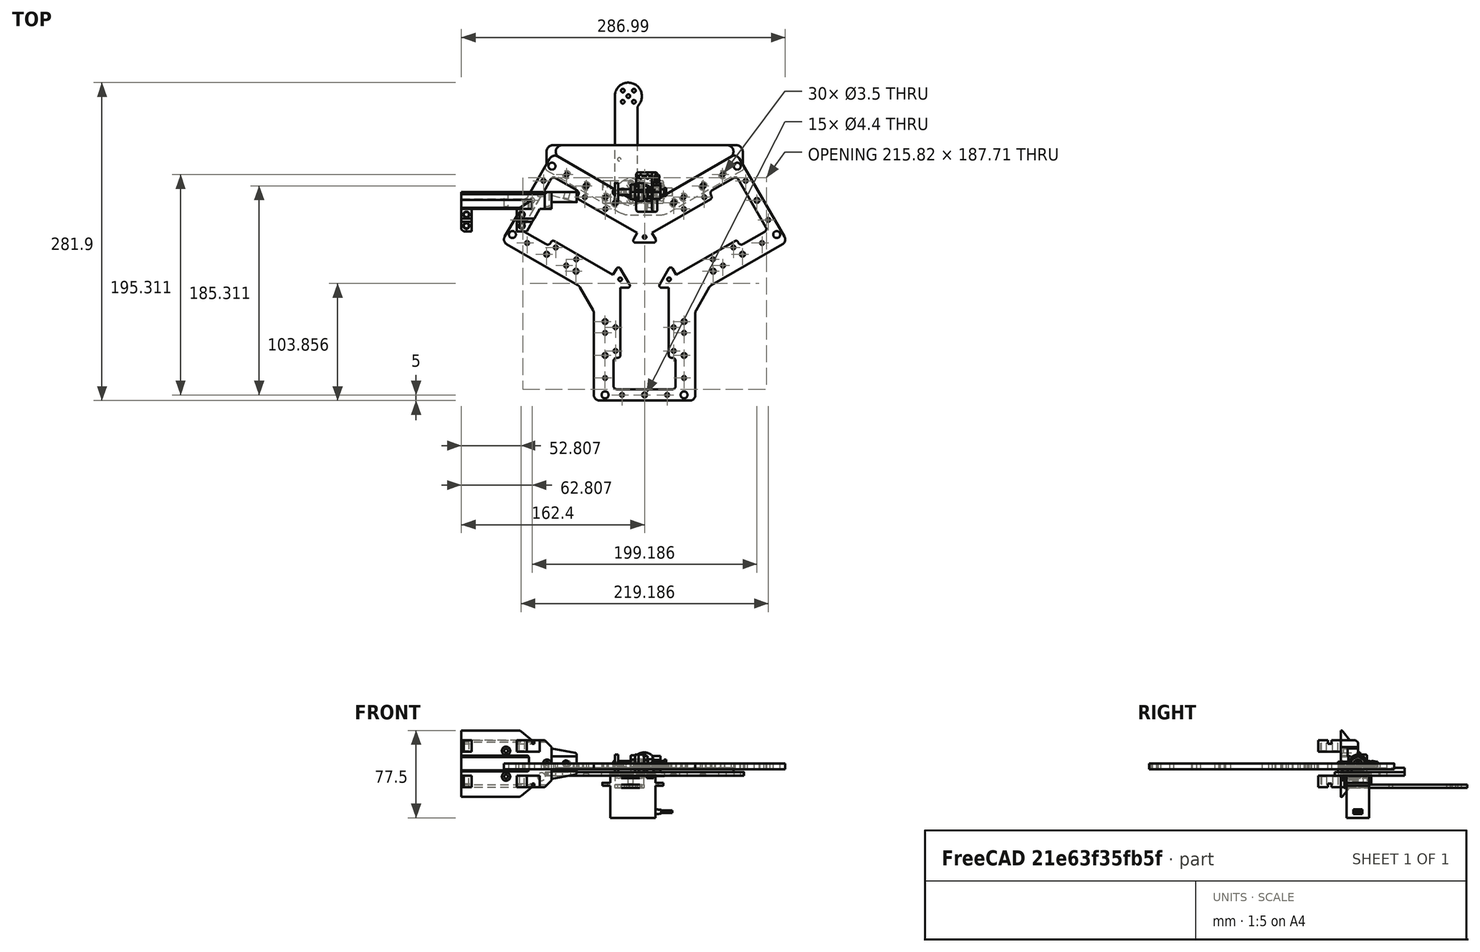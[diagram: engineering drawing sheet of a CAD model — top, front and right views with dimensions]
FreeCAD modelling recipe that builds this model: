
FCSTD DOCUMENT  (FreeCAD 1.2R20260204 (Git shallow))
Label: twin-actuator
License: All rights reserved
LicenseURL: https://en.wikipedia.org/wiki/All_rights_reserved
objects: Sketcher::SketchObject×46, App::Link×38, PartDesign::Pad×24, App::FeaturePython×22, App::Point×19, PartDesign::Pocket×17, PartDesign::Chamfer×17, PartDesign::Fillet×15, PartDesign::Body×13, PartDesign::Draft×6, PartDesign::Revolution×4, Assembly::JointGroup×3, Assembly::AssemblyObject×3, Part::FeaturePython×2, PartDesign::ShapeBinder×2, App::Part×2, PartDesign::SubShapeBinder×2, PartDesign::Mirrored×2, TechDraw::DrawProjGroupItem×2, PartDesign::LinearPattern×1, +5 more types
note: 367 computed .brp shape members not serialized (recipe doc carries the construction recipe); baked Part::Feature solids carry a one-line shape summary decoded from their .brp
EXTERNAL_REF file=linear-lifter.FCStd obj=Assembly
EXTERNAL_REF file=linear-lifter.FCStd obj=MGN9_225mm_Custom
EXTERNAL_REF file=linear-lifter.FCStd obj=ClipRail
EXTERNAL_REF file=linear-lifter.FCStd obj=ClipRail001
EXTERNAL_REF file=linear-lifter.FCStd obj=ClipRail002
EXTERNAL_REF file=linear-lifter.FCStd obj=Chariot
EXTERNAL_REF file=linear-lifter.FCStd obj=mgn9c
EXTERNAL_REF file=linear-lifter.FCStd obj=Body028
EXTERNAL_REF file=linear-lifter.FCStd obj=MF001
EXTERNAL_REF file=linear-lifter.FCStd obj=MF002
EXTERNAL_REF file=linear-lifter.FCStd obj=Bielle001
EXTERNAL_REF file=linear-lifter.FCStd obj=RoundServoHorn
EXTERNAL_REF file=linear-lifter.FCStd obj=ServoLifterSpacer
EXTERNAL_REF file=linear-lifter.FCStd obj=ServoLifterPlate
EXTERNAL_REF file=linear-lifter.FCStd obj=Bielle002
EXTERNAL_REF file=linear-lifter.FCStd obj=MG997
EXTERNAL_REF file=../../ECAD/color-sensor-2026/color-sensor-asm.FCStd obj=Part001

FEATURE [App::Point] Origin133  label="Origine001"
  Role = Origin
FEATURE [App::Point] Origin136  label="Origine004"
  Role = Origin
FEATURE [App::Point] Origin137  label="Origine005"
  Role = Origin
FEATURE [App::Point] Origin138  label="Origine006"
  Role = Origin
FEATURE [Part::FeaturePython] Screw  label="M3x10-Vis"  # WARN: FeaturePython — macro-defined, semantics opaque (R4)
  BaseObject = -> Body [Edge47]
  Diameter = 1
  Invert = false
  LeftHanded = false
  Length = 2
  LengthCustom = 10
  MatchOuter = false
  Offset = 3
  OffsetAngle = 0
  Placement = pos=(-26,-1.72853e-06,-7e-16) rot=(0,-1,0;1.5708rad)
  Thread = false
  Type = 85
FEATURE [Sketcher::SketchObject] Sketch
  ArcFitTolerance = 0
  AttachmentSupport = -> [XZ_Plane]
  ExternalTypes = [0]
  FullyConstrained = true
  MakeInternals = false
  MapMode = 5
  Placement = pos=(0,0,0) rot=(1,0,0;1.5708rad)
  sketch-geometry (14):
    g0: LineSegment StartX=0 StartY=2.5 StartZ=0 EndX=3 EndY=2.5 EndZ=0
    g1: LineSegment StartX=3 StartY=2.5 StartZ=0 EndX=3 EndY=3.5 EndZ=0
    g2: LineSegment StartX=3 StartY=3.5 StartZ=0 EndX=5 EndY=3.5 EndZ=0
    g3: LineSegment StartX=5 StartY=3.5 StartZ=0 EndX=5 EndY=1.5 EndZ=0
    g4: LineSegment StartX=5 StartY=1.5 StartZ=0 EndX=-9 EndY=1.5 EndZ=0
    g5: LineSegment StartX=-9 StartY=1.5 StartZ=0 EndX=-9 EndY=0 EndZ=0
    g6: LineSegment StartX=-9 StartY=0 StartZ=0 EndX=-37.5 EndY=0 EndZ=0
    g7: LineSegment StartX=-37.5 StartY=0 StartZ=0 EndX=-37.5 EndY=2.5 EndZ=0
    g8: LineSegment StartX=-37.5 StartY=2.5 StartZ=0 EndX=-11 EndY=2.5 EndZ=0
    g9: LineSegment StartX=-11 StartY=2.5 StartZ=0 EndX=-11 EndY=4 EndZ=0
    g10: LineSegment StartX=-11 StartY=4 StartZ=0 EndX=-7 EndY=4 EndZ=0
    g11: LineSegment StartX=-7 StartY=4 StartZ=0 EndX=-7 EndY=7.5 EndZ=0
    g12: LineSegment StartX=-7 StartY=7.5 StartZ=0 EndX=0 EndY=7.5 EndZ=0
    g13: LineSegment StartX=0 StartY=7.5 StartZ=0 EndX=0 EndY=2.5 EndZ=0
  constraints (42):
    c: PointOnObject(g0,g-2)
    c: Horizontal(g0)
    c: Coincident(g0,g1)
    c: Coincident(g1,g2)
    c: Horizontal(g2)
    c: Coincident(g2,g3)
    c: Vertical(g3)
    c: Coincident(g3,g4)
    c: Horizontal(g4)
    c: Coincident(g4,g5)
    c: Vertical(g5)
    c: Coincident(g5,g6)
    c: PointOnObject(g6,g-1)
    c: Horizontal(g6)
    c: Coincident(g6,g7)
    c: Vertical(g7)
    c: Coincident(g7,g8)
    c: Horizontal(g8)
    c: Coincident(g8,g9)
    c: Coincident(g9,g10)
    c: Horizontal(g10)
    c: Coincident(g10,g11)
    c: Vertical(g11)
    c: Coincident(g11,g12)
    c: Horizontal(g12)
    c: Coincident(g12,g13)
    c: Coincident(g13,g0)
    c: Vertical(g13)
    c: Vertical(g9)
    c: Vertical(g1)
    c: DistanceY(g2) = 3.5
    c: DistanceX(g2,g2) = 2
    c: DistanceX(g-1,g0) = 3
    c: DistanceY(g0) = 2.5
    c: DistanceX(g4,g4) = 14
    c: DistanceY(g3) = 1.5
    c: DistanceY(g10) = 4
    c: DistanceY(g12) = 7.5
    c: DistanceX(g12,g12) = 7
    c: DistanceX(g10,g10) = 4
    c: DistanceY(g8) = 2.5
    c: DistanceX(g6,g3) = 42.5
FEATURE [PartDesign::Revolution] Revolution
  Angle = 360
  Angle2 = 0
  Axis = (1,0,0)
  Base = (0,0,0)
  FuseOrder = 0
  Placement = pos=(0,0,0) rot=(1,0,0;1.5708rad)
  Profile = -> Sketch
  ReferenceAxis = -> X_Axis
  Refine = true
  Suppressed = false
  Type = 0
FEATURE [Sketcher::SketchObject] Sketch001
  ArcFitTolerance = 0
  AttachmentSupport = -> [YZ_Plane]
  ExternalGeometry = -> [Revolution]
  ExternalTypes = [0]
  FullyConstrained = true
  MakeInternals = false
  MapMode = 5
  Placement = pos=(0,0,0) rot=(0.57735,0.57735,0.57735;2.0944rad)
  sketch-geometry (7):
    g0: LineSegment StartX=6 StartY=3.4641 StartZ=0 EndX=0 EndY=6.9282 EndZ=0
    g1: LineSegment StartX=0 StartY=6.9282 StartZ=0 EndX=-6 EndY=3.4641 EndZ=0
    g2: LineSegment StartX=-6 StartY=3.4641 StartZ=0 EndX=-6 EndY=-3.4641 EndZ=0
    g3: LineSegment StartX=-6 StartY=-3.4641 StartZ=0 EndX=1.8723e-12 EndY=-6.9282 EndZ=0
    g4: LineSegment StartX=1.8723e-12 StartY=-6.9282 StartZ=0 EndX=6 EndY=-3.4641 EndZ=0
    g5: LineSegment StartX=6 StartY=-3.4641 StartZ=0 EndX=6 EndY=3.4641 EndZ=0
    g6: Circle [constr] CenterX=0 CenterY=0 CenterZ=0 NormalX=0 NormalY=0 NormalZ=1 AngleXU=0 Radius=6.9282
  constraints (16):
    c: Coincident(g0,g1)
    c: Coincident(g1,g2)
    c: Coincident(g2,g3)
    c: Coincident(g3,g4)
    c: Coincident(g4,g5)
    c: Coincident(g5,g0)
    c: Equal(g0, g1-g5) x5
    c: PointOnObject(g0,g6)
    c: PointOnObject(g1,g6)
    c: PointOnObject(g2,g6)
    c: PointOnObject(g3,g6)
    c: PointOnObject(g4,g6)
    c: PointOnObject(g5,g6)
    c: Coincident(g6,g-1)
    c: PointOnObject(g0,g-2)
    c: DistanceX(g1,g0) = 12
FEATURE [PartDesign::Pocket] Pocket
  BaseFeature = -> Revolution
  Direction = (-1,0,0)
  Length = 5
  Length2 = 100
  Placement = pos=(0,0,0) rot=(1,0,0;1.5708rad)
  Profile = -> Sketch001
  Refine = true
  SideType = 0
  Suppressed = false
  Type = 1
  Type2 = 0
FEATURE [Sketcher::SketchObject] Sketch002
  ArcFitTolerance = 0
  AttachmentSupport = -> [XZ_Plane]
  ExternalGeometry = -> [Pocket]
  ExternalTypes = [0]
  FullyConstrained = true
  MakeInternals = false
  MapMode = 5
  Placement = pos=(0,0,0) rot=(1,0,0;1.5708rad)
  sketch-geometry (2):
    g0: Circle CenterX=-3.5 CenterY=0 CenterZ=0 NormalX=0 NormalY=0 NormalZ=1 AngleXU=0 Radius=2.5
    g1: LineSegment [constr] StartX=-6e-16 StartY=-3.4641 StartZ=0 EndX=-7 EndY=3.4641 EndZ=0
  constraints (5):
    c: PointOnObject(g0,g-1)
    c: Diameter(g0) = 5
    c: Coincident(g1,g-4)
    c: Coincident(g1,g-3)
    c: PointOnObject(g0,g1)
FEATURE [PartDesign::Pocket] Pocket001
  BaseFeature = -> Pocket
  Direction = (0,1,-2e-16)
  Length = 5
  Length2 = 100
  Placement = pos=(0,0,0) rot=(1,0,0;1.5708rad)
  Profile = -> Sketch002
  Refine = true
  SideType = 2
  Suppressed = false
  Type = 1
  Type2 = 0
FEATURE [PartDesign::Chamfer] Chamfer
  Angle = 45
  Base = -> Pocket001 [Edge14,Edge21]
  BaseFeature = -> Pocket001
  ChamferType = 0
  FlipDirection = false
  Placement = pos=(0,0,0) rot=(1,0,0;1.5708rad)
  Refine = true
  Size = 0.2
  Size2 = 1
  SupportTransform = false
  Suppressed = false
  UseAllEdges = false
FEATURE [Sketcher::SketchObject] Sketch003
  ArcFitTolerance = 0
  AttachmentSupport = -> [Chamfer]
  ExternalTypes = [0]
  FullyConstrained = true
  MakeInternals = false
  MapMode = 5
  Placement = pos=(-37.5,0,0) rot=(0.707107,0,-0.707107;3.14159rad)
  sketch-geometry (1):
    g0: Circle CenterX=0 CenterY=0 CenterZ=0 NormalX=0 NormalY=0 NormalZ=1 AngleXU=0 Radius=1.5
  constraints (2):
    c: Coincident(g0,g-1)
    c: Diameter(g0) = 3
FEATURE [PartDesign::Pocket] Pocket002
  BaseFeature = -> Chamfer
  Direction = (1,0,2e-16)
  Length = 5
  Length2 = 100
  Placement = pos=(0,0,0) rot=(1,0,0;1.5708rad)
  Profile = -> Sketch003
  Refine = true
  SideType = 0
  Suppressed = false
  Type = 0
  Type2 = 0
FEATURE [PartDesign::Body] Body  label="Axe"
  AllowCompound = true
  Group = -> [Sketch,Revolution,Sketch001,Pocket,Sketch002,Pocket001,Chamfer,Sketch003,Pocket002]
  Origin = -> Origin105
  Placement = pos=(14.5,-1.72853e-06,0) rot=(0,0,1;0rad)
  Tip = -> Pocket002
FEATURE [Sketcher::SketchObject] Sketch004
  ArcFitTolerance = 0
  AttachmentSupport = -> [XY_Plane001]
  ExternalTypes = [0]
  FullyConstrained = true
  MakeInternals = false
  MapMode = 5
  sketch-geometry (10):
    g0: LineSegment StartX=-12 StartY=2.5 StartZ=0 EndX=-12 EndY=4 EndZ=0
    g1: LineSegment StartX=-12 StartY=4 StartZ=0 EndX=-2 EndY=4 EndZ=0
    g2: LineSegment StartX=-2 StartY=4 StartZ=0 EndX=-2 EndY=3.25 EndZ=0
    g3: LineSegment StartX=-2 StartY=3.25 StartZ=0 EndX=0 EndY=3.25 EndZ=0
    g4: LineSegment StartX=0 StartY=3.25 StartZ=0 EndX=0 EndY=7.5 EndZ=0
    g5: LineSegment StartX=0 StartY=7.5 StartZ=0 EndX=3 EndY=7.5 EndZ=0
    g6: LineSegment StartX=3 StartY=7.5 StartZ=0 EndX=3 EndY=4 EndZ=0
    g7: LineSegment StartX=-12 StartY=2.5 StartZ=0 EndX=3.5 EndY=2.5 EndZ=0
    g8: LineSegment StartX=3.5 StartY=2.5 StartZ=0 EndX=3.5 EndY=4 EndZ=0
    g9: LineSegment StartX=3.5 StartY=4 StartZ=0 EndX=3 EndY=4 EndZ=0
  constraints (30):
    c: Vertical(g0)
    c: Coincident(g0,g1)
    c: Horizontal(g1)
    c: Coincident(g1,g2)
    c: Coincident(g2,g3)
    c: Horizontal(g3)
    c: Coincident(g3,g4)
    c: Vertical(g4)
    c: Coincident(g4,g5)
    c: Horizontal(g5)
    c: Coincident(g5,g6)
    c: Vertical(g6)
    c: Vertical(g2)
    c: DistanceY(g5) = 7.5
    c: DistanceX(g5,g5) = 3
    c: DistanceX(g1,g1) = 10
    c: DistanceY(g3) = 3.25
    c: DistanceY(g1) = 4
    c: Coincident(g0,g7)
    c: Horizontal(g7)
    c: Coincident(g7,g8)
    c: Vertical(g8)
    c: Coincident(g8,g9)
    c: Coincident(g9,g6)
    c: Horizontal(g9)
    c: DistanceY(g7) = 2.5
    c: PointOnObject(g3,g-2)
    c: DistanceX(g0,g7) = 15.5
    c: DistanceX(g6,g8) = 0.5
    c: DistanceY(g8) = 4
FEATURE [PartDesign::Revolution] Revolution002
  Angle = 360
  Angle2 = 0
  Axis = (1,0,0)
  Base = (0,0,0)
  FuseOrder = 0
  Profile = -> Sketch004
  ReferenceAxis = -> X_Axis001
  Refine = true
  Suppressed = false
  Type = 0
FEATURE [Sketcher::SketchObject] Sketch005
  ArcFitTolerance = 0
  AttachmentSupport = -> [YZ_Plane001]
  ExternalGeometry = -> [Revolution002]
  ExternalTypes = [0]
  FullyConstrained = true
  MakeInternals = false
  MapMode = 5
  Placement = pos=(0,0,0) rot=(0.57735,0.57735,0.57735;2.0944rad)
  sketch-geometry (7):
    g0: LineSegment StartX=0 StartY=6.9282 StartZ=0 EndX=-6 EndY=3.4641 EndZ=0
    g1: LineSegment StartX=-6 StartY=3.4641 StartZ=0 EndX=-6 EndY=-3.4641 EndZ=0
    g2: LineSegment StartX=-6 StartY=-3.4641 StartZ=0 EndX=0 EndY=-6.9282 EndZ=0
    g3: LineSegment StartX=0 StartY=-6.9282 StartZ=0 EndX=6 EndY=-3.4641 EndZ=0
    g4: LineSegment StartX=6 StartY=-3.4641 StartZ=0 EndX=6 EndY=3.4641 EndZ=0
    g5: LineSegment StartX=6 StartY=3.4641 StartZ=0 EndX=0 EndY=6.9282 EndZ=0
    g6: Circle [constr] CenterX=0 CenterY=0 CenterZ=0 NormalX=0 NormalY=0 NormalZ=1 AngleXU=0 Radius=6.9282
  constraints (16):
    c: Coincident(g0,g1)
    c: Coincident(g1,g2)
    c: Coincident(g2,g3)
    c: Coincident(g3,g4)
    c: Coincident(g4,g5)
    c: Coincident(g5,g0)
    c: Equal(g0, g1-g5) x5
    c: PointOnObject(g0,g6)
    c: PointOnObject(g1,g6)
    c: PointOnObject(g2,g6)
    c: PointOnObject(g3,g6)
    c: PointOnObject(g4,g6)
    c: PointOnObject(g5,g6)
    c: Coincident(g6,g-1)
    c: PointOnObject(g5,g-2)
    c: DistanceX(g0,g4) = 12
FEATURE [PartDesign::Pocket] Pocket003
  BaseFeature = -> Revolution002
  Direction = (-1,0,0)
  Length = 5
  Length2 = 100
  Profile = -> Sketch005
  Refine = true
  Reversed = true
  SideType = 0
  Suppressed = false
  Type = 1
  Type2 = 0
FEATURE [PartDesign::Chamfer] Chamfer001
  Angle = 45
  Base = -> Pocket003 [Edge2,Edge5]
  BaseFeature = -> Pocket003
  ChamferType = 0
  FlipDirection = false
  Refine = true
  Size = 0.3
  Size2 = 1
  SupportTransform = false
  Suppressed = false
  UseAllEdges = false
FEATURE [PartDesign::Body] Body001  label="Coulisse"
  AllowCompound = true
  Group = -> [Sketch004,Revolution002,Sketch005,Pocket003,Chamfer001]
  Origin = -> Origin001
  Placement = pos=(-3.8147e-06,9.095e-13,0) rot=(0,0,1;0rad)
  Tip = -> Chamfer001
FEATURE [Sketcher::SketchObject] Sketch006
  ArcFitTolerance = 0
  AttachmentSupport = -> [XY_Plane002]
  ExternalTypes = [0]
  FullyConstrained = true
  MakeInternals = false
  MapMode = 5
  sketch-geometry (10):
    g0: LineSegment StartX=0 StartY=-4.5 StartZ=0 EndX=-2.5 EndY=-4.5 EndZ=0
    g1: LineSegment StartX=-2.5 StartY=-4.5 StartZ=0 EndX=-2.5 EndY=-1 EndZ=0
    g2: LineSegment StartX=-2.5 StartY=-1 StartZ=0 EndX=-2 EndY=-1 EndZ=0
    g3: LineSegment StartX=-2 StartY=-1 StartZ=0 EndX=-2 EndY=0 EndZ=0
    g4: LineSegment StartX=-2 StartY=0 StartZ=0 EndX=-4 EndY=0 EndZ=0
    g5: LineSegment StartX=-4 StartY=0 StartZ=0 EndX=-4 EndY=2.5 EndZ=0
    g6: LineSegment StartX=-4 StartY=2.5 StartZ=0 EndX=-2 EndY=2.5 EndZ=0
    g7: LineSegment StartX=-2 StartY=2.5 StartZ=0 EndX=-2 EndY=3.5 EndZ=0
    g8: LineSegment StartX=-2 StartY=3.5 StartZ=0 EndX=0 EndY=3.5 EndZ=0
    g9: LineSegment StartX=0 StartY=3.5 StartZ=0 EndX=0 EndY=-4.5 EndZ=0
  constraints (30):
    c: Horizontal(g0)
    c: Coincident(g0,g1)
    c: Vertical(g1)
    c: Coincident(g1,g2)
    c: Horizontal(g2)
    c: Coincident(g2,g3)
    c: PointOnObject(g3,g-1)
    c: Vertical(g3)
    c: Coincident(g3,g4)
    c: PointOnObject(g4,g-1)
    c: Coincident(g4,g5)
    c: Vertical(g5)
    c: Coincident(g5,g6)
    c: Horizontal(g6)
    c: Coincident(g6,g7)
    c: Vertical(g7)
    c: Coincident(g7,g8)
    c: Horizontal(g8)
    c: Coincident(g8,g9)
    c: Coincident(g9,g0)
    c: Vertical(g9)
    c: DistanceY(g5) = 2.5
    c: DistanceX(g3,g-1) = 2
    c: DistanceX(g0,g-1) = 2.5
    c: DistanceX(g4,g-1) = 4
    c: DistanceY(g7,g7) = 1
    c: DistanceY(g3,g3) = 1
    c: DistanceY(g0,g6) = 7
    c: DistanceX(g7,g-1) = 2
    c: PointOnObject(g0,g-2)
FEATURE [PartDesign::Revolution] Revolution003
  Angle = 360
  Angle2 = 0
  Axis = (0,1,0)
  Base = (0,0,0)
  FuseOrder = 0
  Profile = -> Sketch006
  ReferenceAxis = -> Sketch006 [V_Axis]
  Refine = true
  Suppressed = false
  Type = 0
FEATURE [Sketcher::SketchObject] Sketch007
  ArcFitTolerance = 0
  AttachmentSupport = -> [XY_Plane002]
  ExternalTypes = [0]
  FullyConstrained = true
  MakeInternals = false
  MapMode = 5
FEATURE [Sketcher::SketchObject] Sketch008
  ArcFitTolerance = 0
  AttachmentSupport = -> [XY_Plane002]
  ExternalGeometry = -> [Revolution003]
  ExternalTypes = [0]
  FullyConstrained = true
  MakeInternals = false
  MapMode = 5
  sketch-geometry (5):
    g0: LineSegment StartX=0 StartY=3.5 StartZ=0 EndX=-2.5 EndY=3.5 EndZ=0
    g1: LineSegment StartX=-2.5 StartY=3.5 StartZ=0 EndX=-2.5 EndY=4.5 EndZ=0
    g2: LineSegment StartX=-2.5 StartY=4.5 StartZ=0 EndX=-2 EndY=6.5 EndZ=0
    g3: LineSegment StartX=-2 StartY=6.5 StartZ=0 EndX=0 EndY=6.5 EndZ=0
    g4: LineSegment StartX=0 StartY=6.5 StartZ=0 EndX=0 EndY=3.5 EndZ=0
  constraints (15):
    c: PointOnObject(g0,g-2)
    c: Horizontal(g0)
    c: Coincident(g0,g1)
    c: Coincident(g1,g2)
    c: Coincident(g2,g3)
    c: PointOnObject(g3,g-2)
    c: Horizontal(g3)
    c: Coincident(g3,g4)
    c: Coincident(g0,g4)
    c: PointOnObject(g0,g-3)
    c: DistanceX(g0,g-1) = 2.5
    c: Vertical(g1)
    c: DistanceY(g4,g4) = 3
    c: DistanceX(g2,g0) = 2
    c: DistanceY(g1,g1) = 1
FEATURE [PartDesign::Revolution] Revolution004
  Angle = 360
  Angle2 = 0
  Axis = (0,1,0)
  Base = (0,0,0)
  BaseFeature = -> Revolution003
  FuseOrder = 0
  Profile = -> Sketch008
  ReferenceAxis = -> Sketch008 [V_Axis]
  Refine = true
  Suppressed = false
  Type = 0
FEATURE [PartDesign::LinearPattern] LinearPattern001
  BaseFeature = -> Revolution004
  Direction = -> Y_Axis002
  Length = 3
  Length2 = 100
  Mode = 0
  Mode2 = 0
  Occurrences = 2
  Occurrences2 = 1
  Offset = 3
  Offset2 = 10
  Originals = -> [Revolution004]
  Refine = true
  Reversed2 = false
  SpacingPattern = [0]
  SpacingPattern2 = [0]
  Spacings = [-1]
  Suppressed = false
  TransformMode = 0
FEATURE [Sketcher::SketchObject] Sketch009
  ArcFitTolerance = 0
  AttachmentSupport = -> [XZ_Plane002]
  ExternalTypes = [0]
  FullyConstrained = true
  MakeInternals = false
  MapMode = 5
  Placement = pos=(0,0,0) rot=(1,0,0;1.5708rad)
  sketch-geometry (1):
    g0: Circle CenterX=0 CenterY=0 CenterZ=0 NormalX=0 NormalY=0 NormalZ=1 AngleXU=0 Radius=1.5
  constraints (2):
    c: Coincident(g0,g-1)
    c: Diameter(g0) = 3
FEATURE [PartDesign::Pocket] Pocket004
  BaseFeature = -> LinearPattern001
  Direction = (0,1,-2e-16)
  Length = 5
  Length2 = 100
  Profile = -> Sketch009
  Refine = true
  SideType = 2
  Suppressed = false
  Type = 1
  Type2 = 0
FEATURE [PartDesign::Chamfer] Chamfer002
  Angle = 45
  Base = -> Pocket004 [Edge1,Edge3]
  BaseFeature = -> Pocket004
  ChamferType = 0
  FlipDirection = false
  Refine = true
  Size = 0.3
  Size2 = 1
  SupportTransform = false
  Suppressed = false
  UseAllEdges = false
FEATURE [Sketcher::SketchObject] Sketch010
  ArcFitTolerance = 0
  AttachmentSupport = -> [XZ_Plane002]
  ExternalGeometry = -> [Chamfer002]
  ExternalTypes = [0]
  FullyConstrained = true
  MakeInternals = false
  MapMode = 5
  Placement = pos=(0,0,0) rot=(1,0,0;1.5708rad)
  sketch-geometry (7):
    g0: LineSegment StartX=0 StartY=3.4641 StartZ=0 EndX=-3 EndY=1.73205 EndZ=0
    g1: LineSegment StartX=-3 StartY=1.73205 StartZ=0 EndX=-3 EndY=-1.73205 EndZ=0
    g2: LineSegment StartX=-3 StartY=-1.73205 StartZ=0 EndX=-5.997e-12 EndY=-3.4641 EndZ=0
    g3: LineSegment StartX=-5.997e-12 StartY=-3.4641 StartZ=0 EndX=3 EndY=-1.73205 EndZ=0
    g4: LineSegment StartX=3 StartY=-1.73205 StartZ=0 EndX=3 EndY=1.73205 EndZ=0
    g5: LineSegment StartX=3 StartY=1.73205 StartZ=0 EndX=0 EndY=3.4641 EndZ=0
    g6: Circle [constr] CenterX=0 CenterY=0 CenterZ=0 NormalX=0 NormalY=0 NormalZ=1 AngleXU=0 Radius=3.4641
  constraints (16):
    c: Coincident(g0,g1)
    c: Coincident(g1,g2)
    c: Coincident(g2,g3)
    c: Coincident(g3,g4)
    c: Coincident(g4,g5)
    c: Coincident(g5,g0)
    c: Equal(g0, g1-g5) x5
    c: PointOnObject(g0,g6)
    c: PointOnObject(g1,g6)
    c: PointOnObject(g2,g6)
    c: PointOnObject(g3,g6)
    c: PointOnObject(g4,g6)
    c: PointOnObject(g5,g6)
    c: Coincident(g6,g-1)
    c: PointOnObject(g0,g-2)
    c: DistanceX(g0,g4) = 6
FEATURE [PartDesign::Pocket] Pocket005
  BaseFeature = -> Chamfer002
  Direction = (0,1,-2e-16)
  Length = 5
  Length2 = 100
  Profile = -> Sketch010
  Refine = true
  SideType = 0
  Suppressed = false
  Type = 1
  Type2 = 0
FEATURE [PartDesign::Body] Body002  label="ConnecteurPneu"
  AllowCompound = true
  Group = -> [Sketch006,Revolution003,Sketch007,Sketch008,Revolution004,LinearPattern001,Sketch009,Pocket004,Chamfer002,Sketch010,Pocket005]
  Origin = -> Origin002
  Placement = pos=(11,6,0) rot=(0,0,1;0rad)
  Tip = -> Pocket005
FEATURE [Sketcher::SketchObject] Sketch013
  ArcFitTolerance = 0
  AttachmentSupport = -> [YZ_Plane005]
  ExternalTypes = [0]
  FullyConstrained = true
  MakeInternals = false
  MapMode = 5
  Placement = pos=(0,0,0) rot=(0.57735,0.57735,0.57735;2.0944rad)
  sketch-geometry (5):
    g0: Circle CenterX=0 CenterY=0 CenterZ=0 NormalX=0 NormalY=0 NormalZ=1 AngleXU=0 Radius=1.6
    g1: ArcOfCircle CenterX=0 CenterY=0 CenterZ=0 NormalX=0 NormalY=0 NormalZ=1 AngleXU=0 Radius=8 StartAngle=0 EndAngle=3.14159
    g2: LineSegment StartX=-8 StartY=1e-15 StartZ=0 EndX=-8 EndY=-8 EndZ=0
    g3: LineSegment StartX=-8 StartY=-8 StartZ=0 EndX=8 EndY=-8 EndZ=0
    g4: LineSegment StartX=8 StartY=-8 StartZ=0 EndX=8 EndY=0 EndZ=0
  constraints (14):
    c: Coincident(g0,g-1)
    c: Diameter(g0) = 3.2
    c: Coincident(g1,g0)
    c: PointOnObject(g1,g-1)
    c: PointOnObject(g1,g-1)
    c: Coincident(g2,g1)
    c: Vertical(g2)
    c: Horizontal(g3)
    c: Coincident(g3,g4)
    c: Coincident(g4,g1)
    c: Vertical(g4)
    c: Coincident(g2,g3)
    c: Diameter(g1) = 16
    c: DistanceY(g3) = -8
FEATURE [PartDesign::Pad] Pad002
  Direction = (1,0,0)
  Length = 3
  Length2 = 100
  Placement = pos=(0,0,0) rot=(0.57735,0.57735,0.57735;2.0944rad)
  Profile = -> Sketch013
  Refine = true
  SideType = 0
  Suppressed = false
  Type = 0
  Type2 = 0
FEATURE [PartDesign::Fillet] Fillet001
  Base = -> Pad002 [Edge8,Edge5]
  BaseFeature = -> Pad002
  Placement = pos=(0,0,0) rot=(0.57735,0.57735,0.57735;2.0944rad)
  Radius = 1
  Refine = true
  SupportTransform = false
  Suppressed = false
  UseAllEdges = false
FEATURE [PartDesign::Body] Body004  label="ContreRotation"
  AllowCompound = true
  Group = -> [Sketch013,Pad002,Fillet001]
  Origin = -> Origin006
  Placement = pos=(-26,-2.62261e-06,3.05176e-05) rot=(1,0,0;1.5708rad)
  Tip = -> Fillet001
FEATURE [App::Point] Origin140  label="Origine007"
  Role = Origin
FEATURE [Sketcher::SketchObject] Sketch014
  ArcFitTolerance = 0
  AttachmentSupport = -> [YZ_Plane087]
  ExternalTypes = [0]
  FullyConstrained = true
  MakeInternals = false
  MapMode = 5
  Placement = pos=(0,0,0) rot=(0.57735,0.57735,0.57735;2.0944rad)
  sketch-geometry (5):
    g0: ArcOfCircle CenterX=0 CenterY=0 CenterZ=0 NormalX=0 NormalY=0 NormalZ=1 AngleXU=0 Radius=8 StartAngle=2e-16 EndAngle=3.14159
    g1: LineSegment StartX=-8 StartY=4.01e-14 StartZ=0 EndX=-8 EndY=-8 EndZ=0
    g2: LineSegment StartX=-8 StartY=-8 StartZ=0 EndX=8 EndY=-8 EndZ=0
    g3: LineSegment StartX=8 StartY=-8 StartZ=0 EndX=8 EndY=1.8e-15 EndZ=0
    g4: Circle CenterX=0 CenterY=0 CenterZ=0 NormalX=0 NormalY=0 NormalZ=1 AngleXU=0 Radius=4.15
  constraints (14):
    c: Coincident(g0,g-1)
    c: PointOnObject(g0,g-1)
    c: PointOnObject(g0,g-1)
    c: Coincident(g1,g0)
    c: Coincident(g1,g2)
    c: Horizontal(g2)
    c: Coincident(g2,g3)
    c: Coincident(g3,g0)
    c: Vertical(g3)
    c: Vertical(g1)
    c: Diameter(g0) = 16
    c: DistanceY(g2) = -8
    c: Coincident(g4,g0)
    c: Diameter(g4) = 8.3
FEATURE [PartDesign::Pad] Pad003
  Direction = (1,0,0)
  Length = 8
  Length2 = 100
  Placement = pos=(0,0,0) rot=(0.57735,0.57735,0.57735;2.0944rad)
  Profile = -> Sketch014
  ReferenceAxis = -> Sketch014 [N_Axis]
  Refine = true
  Reversed = true
  SideType = 0
  Suppressed = false
  Type = 0
  Type2 = 0
FEATURE [Sketcher::SketchObject] Sketch015
  ArcFitTolerance = 0
  AttachmentSupport = -> [Pad003]
  ExternalGeometry = -> [Pad003]
  ExternalTypes = [0]
  FullyConstrained = true
  MakeInternals = false
  MapMode = 5
  Placement = pos=(0,-1.8e-15,-8) rot=(0.707107,0.707107,0;3.14159rad)
  sketch-geometry (19):
    g0: LineSegment StartX=-8 StartY=-26 StartZ=0 EndX=8 EndY=-26 EndZ=0
    g1: Circle [constr] CenterX=0 CenterY=-12 CenterZ=0 NormalX=0 NormalY=0 NormalZ=1 AngleXU=0 Radius=10
    g2: LineSegment [constr] StartX=-8 StartY=0 StartZ=0 EndX=8 EndY=0 EndZ=0
    g3: LineSegment StartX=-8 StartY=0 StartZ=0 EndX=-8 EndY=-3.05573 EndZ=0
    g4: LineSegment StartX=8 StartY=0 StartZ=0 EndX=8 EndY=-3.05573 EndZ=0
    g5: LineSegment StartX=8 StartY=-26 StartZ=0 EndX=8 EndY=-20.9443 EndZ=0
    g6: LineSegment StartX=-8 StartY=-26 StartZ=0 EndX=-8 EndY=-20.9443 EndZ=0
    g7: ArcOfCircle CenterX=0 CenterY=-12 CenterZ=0 NormalX=0 NormalY=0 NormalZ=1 AngleXU=0 Radius=12 StartAngle=2.30052 EndAngle=3.98266
    g8: ArcOfCircle CenterX=0 CenterY=-12 CenterZ=0 NormalX=0 NormalY=0 NormalZ=1 AngleXU=0 Radius=12 StartAngle=5.44212 EndAngle=7.12425
    g9: Circle CenterX=-7 CenterY=-12 CenterZ=0 NormalX=0 NormalY=0 NormalZ=1 AngleXU=0 Radius=2.25
    g10: Circle CenterX=7 CenterY=-12 CenterZ=0 NormalX=0 NormalY=0 NormalZ=1 AngleXU=0 Radius=2.25
    g11: Circle [constr] CenterX=0 CenterY=-19 CenterZ=0 NormalX=0 NormalY=0 NormalZ=1 AngleXU=0 Radius=2.25
    g12: Circle [constr] CenterX=0 CenterY=-5 CenterZ=0 NormalX=0 NormalY=0 NormalZ=1 AngleXU=0 Radius=2.25
    g13: Circle [constr] CenterX=0 CenterY=-12 CenterZ=0 NormalX=0 NormalY=0 NormalZ=1 AngleXU=0 Radius=7
    g14: LineSegment [constr] StartX=-7 StartY=-12 StartZ=0 EndX=7 EndY=-12 EndZ=0
    g15: Circle [constr] CenterX=0 CenterY=-12 CenterZ=0 NormalX=0 NormalY=0 NormalZ=1 AngleXU=0 Radius=2.25
    g16: LineSegment StartX=-8 StartY=0 StartZ=0 EndX=-8 EndY=18 EndZ=0
    g17: LineSegment StartX=-8 StartY=18 StartZ=0 EndX=8 EndY=18 EndZ=0
    g18: LineSegment StartX=8 StartY=18 StartZ=0 EndX=8 EndY=0 EndZ=0
  constraints (51):
    c: Symmetric(g0,g0,g-2)
    c: DistanceY(g0,g-1) = 26
    c: PointOnObject(g1,g-2)
    c: DistanceY(g1,g-1) = 12
    c: Diameter(g1) = 20
    c: PointOnObject(g2,g-1)
    c: Equal(g0,g2)
    c: Symmetric(g2,g2,g-2)
    c: Coincident(g2,g3)
    c: Vertical(g3)
    c: Coincident(g2,g4)
    c: Vertical(g4)
    c: Coincident(g0,g5)
    c: Vertical(g5)
    c: Coincident(g0,g6)
    c: Vertical(g6)
    c: Coincident(g7,g1)
    c: Coincident(g7,g3)
    c: Coincident(g7,g6)
    c: Coincident(g8,g7)
    c: Coincident(g8,g4)
    c: Coincident(g8,g5)
    c: DistanceX(g2,g2) = 16
    c: Diameter(g8) = 24
    c: PointOnObject(g11,g-2)
    c: PointOnObject(g12,g-2)
    c: Coincident(g13,g7)
    c: PointOnObject(g12,g13)
    c: PointOnObject(g10,g13)
    c: PointOnObject(g11,g13)
    c: PointOnObject(g9,g13)
    c: Diameter(g13) = 14
    c: Diameter(g12) = 4.5
    c: Equal(g12,g11)
    c: Equal(g12,g10)
    c: Equal(g12,g9)
    c: Coincident(g14,g9)
    c: Coincident(g14,g10)
    c: Horizontal(g14)
    c: PointOnObject(g7,g14)
    c: Equal(g3,g4)
    c: Coincident(g15,g7)
    c: Equal(g15,g10)
    c: Coincident(g16,g2)
    c: Vertical(g16)
    c: Coincident(g17,g16)
    c: Horizontal(g17)
    c: Coincident(g18,g17)
    c: Coincident(g18,g2)
    c: Vertical(g18)
    c: DistanceY(g18,g18) = 18
FEATURE [PartDesign::Pad] Pad004
  BaseFeature = -> Pad003
  Direction = (0,0,-1)
  Length = 10.5
  Length2 = 100
  Placement = pos=(0,0,0) rot=(0.57735,0.57735,0.57735;2.0944rad)
  Profile = -> Sketch015
  ReferenceAxis = -> Sketch015 [N_Axis]
  Refine = true
  SideType = 0
  Suppressed = false
  Type = 0
  Type2 = 0
FEATURE [PartDesign::Chamfer] Chamfer004
  Angle = 45
  Base = -> Pad004 [Edge20,Edge21,Edge38,Edge39]
  BaseFeature = -> Pad004
  ChamferType = 0
  FlipDirection = false
  Placement = pos=(0,0,0) rot=(0.57735,0.57735,0.57735;2.0944rad)
  Refine = true
  Size = 0.4
  Size2 = 1
  SupportTransform = false
  Suppressed = false
  UseAllEdges = false
FEATURE [PartDesign::Fillet] Fillet002
  Base = -> Chamfer004 [Edge35,Edge13,Edge28,Edge22,Edge20,Edge18,Edge16,Edge14]
  BaseFeature = -> Chamfer004
  Placement = pos=(0,0,0) rot=(0.57735,0.57735,0.57735;2.0944rad)
  Radius = 3
  Refine = true
  SupportTransform = false
  Suppressed = false
  UseAllEdges = false
FEATURE [Part::FeaturePython] Nut001  label="M8-Écrou004"  # WARN: FeaturePython — macro-defined, semantics opaque (R4)
  Diameter = 9
  Invert = true
  LeftHanded = false
  MatchOuter = false
  Offset = 5
  OffsetAngle = 0
  Placement = pos=(-8,3.3e-15,-2.8e-15) rot=(0,1,0;4.71239rad)
  Thread = false
  Type = 34
FEATURE [App::Point] Origin145  label="Origine012"
  Role = Origin
FEATURE [App::Point] Origin147  label="Origine014"
  Role = Origin
FEATURE [App::Link] SupportBras  label="SupportBras001"
  LinkPlacement = pos=(-79.6462,173.8,8.60566) rot=(-0.17215,0.356817,0.918175;3.59264rad)
  LinkedObject = -> Body005
  Placement = pos=(-79.6462,173.8,8.60566) rot=(-0.17215,0.356817,0.918175;3.59264rad)
FEATURE [App::Link] M8_Écrou004  label="M8-Écrou005"
  LinkPlacement = pos=(-69.522,180.003,10.343) rot=(0.617012,-0.780266,-0.102382;1.72836rad)
  LinkedObject = -> Nut001
  Placement = pos=(-69.522,180.003,10.343) rot=(0.617012,-0.780266,-0.102382;1.72836rad)
FEATURE [App::Link] Coulisse  label="Coulisse001"
  LinkPlacement = pos=(-79.6462,173.8,8.60566) rot=(-0.304533,-0.169428,0.937312;4.26313rad)
  LinkedObject = -> Body001
  Placement = pos=(-79.6462,173.8,8.60566) rot=(-0.304533,-0.169428,0.937312;4.26313rad)
FEATURE [App::Link] ConnecteurPneu  label="ConnecteurPneu001"
  LinkPlacement = pos=(-73.7107,180.292,16.9935) rot=(-0.215277,0.690739,0.690316;3.56562rad)
  LinkedObject = -> Body002
  Placement = pos=(-73.7107,180.292,16.9935) rot=(-0.215277,0.690739,0.690316;3.56562rad)
FEATURE [App::Link] Axe  label="Axe001"
  LinkPlacement = pos=(-70.8294,182.278,10.993) rot=(0.915071,0.285192,-0.285151;4.62314rad)
  LinkedObject = -> Body
  Placement = pos=(-70.8294,182.278,10.993) rot=(0.915071,0.285192,-0.285151;4.62314rad)
FEATURE [App::Link] ContreRotation  label="ContreRotation001"
  LinkPlacement = pos=(-101.687,160.969,10.998) rot=(-2.2e-05,0.000306,1;3.74597rad)
  LinkedObject = -> Body004
  Placement = pos=(-101.687,160.969,10.998) rot=(-2.2e-05,0.000306,1;3.74597rad)
FEATURE [App::Link] M3x10_Vis  label="M3x10-Vis001"
  LinkPlacement = pos=(-104.155,159.264,10.9984) rot=(0.802998,-0.421624,-0.421222;1.78804rad)
  LinkedObject = -> Screw
  Placement = pos=(-104.155,159.264,10.9984) rot=(0.802998,-0.421624,-0.421222;1.78804rad)
FEATURE [PartDesign::ShapeBinder] ShapeBinder
  Placement = pos=(3.5e-15,-1.2e-15,-10.5) rot=(0,0,1;0rad)
  Support = -> [Fillet002]
  TraceSupport = false
FEATURE [Sketcher::SketchObject] Sketch016
  ArcFitTolerance = 1e-06
  AttachmentSupport = -> [ShapeBinder]
  ExternalGeometry = -> [ShapeBinder]
  ExternalTypes = [0,0,0]
  FullyConstrained = true
  MakeInternals = false
  MapMode = 5
  Placement = pos=(3.5e-15,-1.2e-15,-18.5) rot=(1,0,0;3.14159rad)
  sketch-geometry (2):
    g0: Circle CenterX=-12 CenterY=7 CenterZ=0 NormalX=0 NormalY=0 NormalZ=1 AngleXU=0 Radius=1.6
    g1: Circle CenterX=-12 CenterY=-7 CenterZ=0 NormalX=0 NormalY=0 NormalZ=1 AngleXU=0 Radius=1.6
  constraints (4):
    c: Coincident(g0,g-21)
    c: Coincident(g1,g-22)
    c: Equal(g1,g0)
    c: Diameter(g0) = 3.2
FEATURE [PartDesign::Pad] Pad005
  Direction = (0,0,-1)
  Length = 3
  Length2 = 10
  Placement = pos=(3.5e-15,-1.2e-15,-10.5) rot=(0,0,1;0rad)
  Profile = -> Sketch016
  ReferenceAxis = -> Sketch016 [N_Axis]
  Refine = true
  SideType = 0
  Suppressed = false
  Type = 0
  Type2 = 0
FEATURE [Sketcher::SketchObject] Sketch017
  ArcFitTolerance = 1e-06
  AttachmentSupport = -> [Pad005]
  ExternalGeometry = -> [Pad005]
  ExternalTypes = [0,0,0]
  FullyConstrained = true
  MakeInternals = false
  MapMode = 5
  Placement = pos=(3.5e-15,-1.2e-15,-21.5) rot=(1,0,0;3.14159rad)
  sketch-geometry (16):
    g0: LineSegment StartX=-26 StartY=-5 StartZ=0 EndX=-26 EndY=-85 EndZ=0
    g1: LineSegment StartX=-6 StartY=-10.3923 StartZ=0 EndX=-6 EndY=-76.0557 EndZ=0
    g2: ArcOfCircle CenterX=-12 CenterY=-9e-16 CenterZ=0 NormalX=0 NormalY=0 NormalZ=1 AngleXU=0 Radius=12 StartAngle=3.57137 EndAngle=5.23599
    g3: LineSegment StartX=-22.9087 StartY=-5 StartZ=0 EndX=-26 EndY=-5 EndZ=0
    g4: ArcOfCircle CenterX=-14 CenterY=-85 CenterZ=0 NormalX=0 NormalY=0 NormalZ=1 AngleXU=0 Radius=12 StartAngle=3.14159 EndAngle=7.12425
    g5: Circle CenterX=-14 CenterY=-85 CenterZ=0 NormalX=0 NormalY=0 NormalZ=1 AngleXU=0 Radius=1.6
    g6: Circle [constr] CenterX=-14 CenterY=-85 CenterZ=0 NormalX=0 NormalY=0 NormalZ=1 AngleXU=0 Radius=7
    g7: LineSegment [constr] StartX=-9.05025 StartY=-80.0503 StartZ=0 EndX=-18.9497 EndY=-80.0503 EndZ=0
    g8: LineSegment [constr] StartX=-18.9497 StartY=-80.0503 StartZ=0 EndX=-18.9497 EndY=-89.9497 EndZ=0
    g9: LineSegment [constr] StartX=-18.9497 StartY=-89.9497 StartZ=0 EndX=-9.05025 EndY=-89.9497 EndZ=0
    g10: LineSegment [constr] StartX=-9.05025 StartY=-89.9497 StartZ=0 EndX=-9.05025 EndY=-80.0503 EndZ=0
    g11: Circle [constr] CenterX=-14 CenterY=-85 CenterZ=0 NormalX=0 NormalY=0 NormalZ=1 AngleXU=0 Radius=7
    g12: Circle CenterX=-18.9497 CenterY=-80.0503 CenterZ=0 NormalX=0 NormalY=0 NormalZ=1 AngleXU=0 Radius=1.6
    g13: Circle CenterX=-9.05025 CenterY=-80.0503 CenterZ=0 NormalX=0 NormalY=0 NormalZ=1 AngleXU=0 Radius=1.6
    g14: Circle CenterX=-9.05025 CenterY=-89.9497 CenterZ=0 NormalX=0 NormalY=0 NormalZ=1 AngleXU=0 Radius=1.6
    g15: Circle CenterX=-18.9497 CenterY=-89.9497 CenterZ=0 NormalX=0 NormalY=0 NormalZ=1 AngleXU=0 Radius=1.6
  constraints (40):
    c: Coincident(g0,g-3)
    c: Vertical(g0)
    c: PointOnObject(g1,g-4)
    c: Vertical(g1)
    c: Coincident(g2,g-4)
    c: Coincident(g2,g1)
    c: Coincident(g3,g2)
    c: Coincident(g3,g0)
    c: Horizontal(g3)
    c: Coincident(g4,g1)
    c: Tangent(g4,g0) = -1.5708
    c: Radius(g4) = 12
    c: Distance(g0,g1) = 20
    c: DistanceY(g4,g2) = 85
    c: Coincident(g5,g4)
    c: Coincident(g6,g4)
    c: Diameter(g5) = 3.2
    c: Coincident(g7,g8)
    c: Coincident(g8,g9)
    c: Coincident(g9,g10)
    c: Coincident(g10,g7)
    c: Equal(g7,g8)
    c: Equal(g7,g9)
    c: Equal(g7,g10)
    c: PointOnObject(g7,g11)
    c: PointOnObject(g8,g11)
    c: PointOnObject(g9,g11)
    c: PointOnObject(g10,g11)
    c: Coincident(g11,g4)
    c: PointOnObject(g10,g6)
    c: Horizontal(g7)
    c: Coincident(g12,g7)
    c: Coincident(g13,g7)
    c: Coincident(g14,g9)
    c: Coincident(g15,g8)
    c: Equal(g15,g14)
    c: Equal(g14,g13)
    c: Equal(g13,g12)
    c: Equal(g12,g5)
    c: Diameter(g6) = 14
FEATURE [PartDesign::Pad] Pad006
  BaseFeature = -> Pad005
  Direction = (0,0,-1)
  Length = 3
  Length2 = 10
  Placement = pos=(3.5e-15,-1.2e-15,-10.5) rot=(0,0,1;0rad)
  Profile = -> Sketch017
  ReferenceAxis = -> Sketch017 [N_Axis]
  Refine = true
  Reversed = true
  SideType = 0
  Suppressed = false
  Type = 0
  Type2 = 0
FEATURE [PartDesign::Fillet] Fillet003
  Base = -> Pad006 [Edge26,Edge38]
  BaseFeature = -> Pad006
  Placement = pos=(3.5e-15,-1.2e-15,-10.5) rot=(0,0,1;0rad)
  Radius = 6
  Refine = true
  SupportTransform = false
  Suppressed = false
  UseAllEdges = false
FEATURE [App::Link] arm_plate  label="arm-plate001"
  LinkPlacement = pos=(-74.8464,158.801,10.5635) rot=(-0.150356,-0.119638,0.981366;3.67771rad)
  LinkedObject = -> Body006
  Placement = pos=(-74.8464,158.801,10.5635) rot=(-0.150356,-0.119638,0.981366;3.67771rad)
FEATURE [App::Point] Origin081  label="Origine016"
  Role = Origin
FEATURE [App::Point] Origin082  label="Origine017"
  Role = Origin
FEATURE [App::Point] Origin083  label="Origine018"
  Role = Origin
FEATURE [Sketcher::SketchObject] Sketch086
  ArcFitTolerance = 0
  ExternalTypes = [0]
  FullyConstrained = true
  MakeInternals = false
  MapMode = 5
  Placement = pos=(0,0,0) rot=(1,0,0;1.5708rad)
  sketch-geometry (12):
    g0: LineSegment StartX=-37 StartY=-18.5 StartZ=0 EndX=-37 EndY=-16 EndZ=0
    g1: LineSegment StartX=-37 StartY=-16 StartZ=0 EndX=-30 EndY=-16 EndZ=0
    g2: LineSegment StartX=-30 StartY=-16 StartZ=0 EndX=-30 EndY=-8 EndZ=0
    g3: LineSegment StartX=-30 StartY=-8 StartZ=0 EndX=10 EndY=-8 EndZ=0
    g4: LineSegment StartX=10 StartY=-8 StartZ=0 EndX=10 EndY=-16 EndZ=0
    g5: LineSegment StartX=10 StartY=-16 StartZ=0 EndX=17 EndY=-16 EndZ=0
    g6: LineSegment StartX=17 StartY=-16 StartZ=0 EndX=17 EndY=-18.5 EndZ=0
    g7: LineSegment StartX=17 StartY=-18.5 StartZ=0 EndX=10 EndY=-18.5 EndZ=0
    g8: LineSegment StartX=10 StartY=-18.5 StartZ=0 EndX=10 EndY=-47 EndZ=0
    g9: LineSegment StartX=10 StartY=-47 StartZ=0 EndX=-30 EndY=-47 EndZ=0
    g10: LineSegment StartX=-30 StartY=-47 StartZ=0 EndX=-30 EndY=-18.5 EndZ=0
    g11: LineSegment StartX=-30 StartY=-18.5 StartZ=0 EndX=-37 EndY=-18.5 EndZ=0
  constraints (33):
    c: Vertical(g0)
    c: Coincident(g0,g1)
    c: Horizontal(g1)
    c: Coincident(g1,g2)
    c: Vertical(g2)
    c: Coincident(g2,g3)
    c: Horizontal(g3)
    c: Coincident(g3,g4)
    c: Coincident(g4,g5)
    c: Coincident(g5,g6)
    c: Vertical(g6)
    c: Coincident(g6,g7)
    c: Horizontal(g7)
    c: Coincident(g7,g8)
    c: Vertical(g8)
    c: Coincident(g8,g9)
    c: Horizontal(g9)
    c: Coincident(g9,g10)
    c: Coincident(g10,g11)
    c: Coincident(g11,g0)
    c: Horizontal(g11)
    c: Tangent(g4,g8) = -1.5708
    c: Tangent(g10,g2)
    c: Equal(g1,g5)
    c: Tangent(g1,g5)
    c: Equal(g6,g0)
    c: DistanceX(g-1,g3) = 10
    c: DistanceX(g0,g5) = 54
    c: DistanceX(g10,g7) = 40
    c: DistanceY(g9,g-1) = 47
    c: DistanceY(g3,g-1) = 8
    c: DistanceY(g6,g6) = 2.5
    c: DistanceY(g0,g-1) = 18.5
FEATURE [PartDesign::Pad] Pad050
  Direction = (0,-1,0)
  Length = 20
  Length2 = 100
  Placement = pos=(0,0,0) rot=(1,0,0;1.5708rad)
  Profile = -> Sketch086
  Refine = true
  SideType = 2
  Suppressed = false
  Type = 0
  Type2 = 0
FEATURE [Sketcher::SketchObject] Sketch087
  ArcFitTolerance = 0
  ExternalTypes = [0]
  FullyConstrained = true
  MakeInternals = false
  MapMode = 5
  sketch-geometry (4):
    g0: Circle CenterX=14.5 CenterY=5 CenterZ=0 NormalX=0 NormalY=0 NormalZ=1 AngleXU=0 Radius=2
    g1: Circle CenterX=14.5 CenterY=-5 CenterZ=0 NormalX=0 NormalY=0 NormalZ=1 AngleXU=0 Radius=2
    g2: Circle CenterX=-34.5 CenterY=5 CenterZ=0 NormalX=0 NormalY=0 NormalZ=1 AngleXU=0 Radius=2
    g3: Circle CenterX=-34.5 CenterY=-5 CenterZ=0 NormalX=0 NormalY=0 NormalZ=1 AngleXU=0 Radius=2
  constraints (10):
    c: Equal(g2,g3)
    c: Equal(g3,g1)
    c: Equal(g1,g0)
    c: Symmetric(g0,g1,g-1)
    c: Symmetric(g2,g3,g-1)
    c: Horizontal(g2,g0)
    c: Diameter(g0) = 4
    c: DistanceY(g1,g0) = 10
    c: DistanceX(g2,g0) = 49
    c: DistanceX(g-1,g0) = 14.5
FEATURE [PartDesign::Pocket] Pocket033
  BaseFeature = -> Pad050
  Direction = (0,0,-1)
  Length = 5
  Length2 = 100
  Placement = pos=(0,0,0) rot=(1,0,0;1.5708rad)
  Profile = -> Sketch087
  Refine = true
  SideType = 0
  Suppressed = false
  Type = 1
  Type2 = 0
FEATURE [PartDesign::Fillet] Fillet024
  Base = -> Pocket033 [Edge28,Edge19,Edge4,Edge3]
  BaseFeature = -> Pocket033
  Placement = pos=(0,0,0) rot=(1,0,0;1.5708rad)
  Radius = 1
  Refine = true
  SupportTransform = false
  Suppressed = false
  UseAllEdges = false
FEATURE [Sketcher::SketchObject] Sketch088
  ArcFitTolerance = 0
  ExternalTypes = [0]
  FullyConstrained = true
  MakeInternals = false
  MapMode = 5
  sketch-geometry (7):
    g0: Circle CenterX=0 CenterY=0 CenterZ=0 NormalX=0 NormalY=0 NormalZ=1 AngleXU=0 Radius=10
    g1: Circle CenterX=0 CenterY=7 CenterZ=0 NormalX=0 NormalY=0 NormalZ=1 AngleXU=0 Radius=1.5
    g2: Circle CenterX=7 CenterY=0 CenterZ=0 NormalX=0 NormalY=0 NormalZ=1 AngleXU=0 Radius=1.5
    g3: Circle CenterX=0 CenterY=-7 CenterZ=0 NormalX=0 NormalY=0 NormalZ=1 AngleXU=0 Radius=1.5
    g4: Circle CenterX=-7 CenterY=0 CenterZ=0 NormalX=0 NormalY=0 NormalZ=1 AngleXU=0 Radius=1.5
    g5: Circle [constr] CenterX=0 CenterY=0 CenterZ=0 NormalX=0 NormalY=0 NormalZ=1 AngleXU=0 Radius=7
    g6: Circle CenterX=0 CenterY=0 CenterZ=0 NormalX=0 NormalY=0 NormalZ=1 AngleXU=0 Radius=1.5
  constraints (18):
    c: Coincident(g0,g-1)
    c: Diameter(g0) = 20
    c: PointOnObject(g1,g-2)
    c: PointOnObject(g2,g-1)
    c: PointOnObject(g3,g-2)
    c: PointOnObject(g4,g-1)
    c: Equal(g4,g1)
    c: Equal(g1,g2)
    c: Equal(g2,g3)
    c: Diameter(g1) = 3
    c: Coincident(g5,g0)
    c: PointOnObject(g1,g5)
    c: PointOnObject(g2,g5)
    c: PointOnObject(g3,g5)
    c: PointOnObject(g4,g5)
    c: DistanceX(g4,g2) = 14
    c: Coincident(g6,g0)
    c: Equal(g2,g6)
FEATURE [PartDesign::Pad] Pad052
  Direction = (0,0,1)
  Length = 2
  Length2 = 100
  Profile = -> Sketch088
  Refine = true
  Reversed = true
  SideType = 0
  Suppressed = false
  Type = 0
  Type2 = 0
FEATURE [Sketcher::SketchObject] Sketch089
  ArcFitTolerance = 0
  ExternalTypes = [0]
  FullyConstrained = true
  MakeInternals = false
  MapMode = 5
  sketch-geometry (2):
    g0: Circle CenterX=0 CenterY=0 CenterZ=0 NormalX=0 NormalY=0 NormalZ=1 AngleXU=0 Radius=4.7
    g1: Circle CenterX=0 CenterY=0 CenterZ=0 NormalX=0 NormalY=0 NormalZ=1 AngleXU=0 Radius=3
  constraints (4):
    c: Coincident(g0,g-1)
    c: Coincident(g1,g0)
    c: Diameter(g0) = 9.4
    c: Diameter(g1) = 6
FEATURE [PartDesign::Pad] Pad051
  BaseFeature = -> Pad052
  Direction = (0,0,1)
  Length = 5.4
  Length2 = 100
  Profile = -> Sketch089
  Refine = true
  Reversed = true
  SideType = 0
  Suppressed = false
  Type = 0
  Type2 = 0
FEATURE [PartDesign::Body] Body042  label="RoundServoHorn"
  AllowCompound = true
  Group = -> [Sketch088,Pad052,Sketch089,Pad051]
  Origin = -> Origin063
  Placement = pos=(0,0,0) rot=(1,0,0;1.5708rad)
  Tip = -> Pad051
FEATURE [Sketcher::SketchObject] Sketch090
  ArcFitTolerance = 0
  AttachmentOffset = pos=(0,0,-2) rot=(0,0,1;0rad)
  ExternalTypes = [0]
  FullyConstrained = true
  MakeInternals = false
  MapMode = 5
  Placement = pos=(0,0,-2) rot=(0,0,1;0rad)
  sketch-geometry (1):
    g0: Circle CenterX=0 CenterY=0 CenterZ=0 NormalX=0 NormalY=0 NormalZ=1 AngleXU=0 Radius=3
  constraints (2):
    c: Coincident(g0,g-1)
    c: Diameter(g0) = 6
FEATURE [PartDesign::Pad] Pad053
  Direction = (0,0,1)
  Length = 10
  Length2 = 100
  Placement = pos=(0,0,-2) rot=(0,0,1;0rad)
  Profile = -> Sketch090
  Refine = true
  Reversed = true
  SideType = 0
  Suppressed = false
  Type = 0
  Type2 = 0
FEATURE [PartDesign::Chamfer] Chamfer029
  Angle = 45
  Base = -> Pad053 [Edge2]
  BaseFeature = -> Pad053
  ChamferType = 0
  FlipDirection = false
  Placement = pos=(0,0,-2) rot=(0,0,1;0rad)
  Refine = true
  Size = 0.5
  Size2 = 1
  SupportTransform = false
  Suppressed = false
  UseAllEdges = false
FEATURE [PartDesign::Body] Body043  label="ServoAxis001"
  AllowCompound = true
  Group = -> [Sketch090,Pad053,Chamfer029]
  Origin = -> Origin064
  Tip = -> Chamfer029
FEATURE [Sketcher::SketchObject] Sketch235
  ArcFitTolerance = 0
  AttachmentSupport = -> [Fillet024]
  ExternalTypes = [0]
  FullyConstrained = true
  MakeInternals = false
  MapMode = 5
  Placement = pos=(0,9e-16,-8) rot=(0,0,1;3.14159rad)
  sketch-geometry (1):
    g0: Circle CenterX=0 CenterY=0 CenterZ=0 NormalX=0 NormalY=0 NormalZ=1 AngleXU=0 Radius=6.5
  constraints (2):
    c: Coincident(g0,g-1)
    c: Diameter(g0) = 13
FEATURE [PartDesign::Pad] Pad096
  BaseFeature = -> Fillet024
  Direction = (0,0,1)
  Length = 2
  Length2 = 10
  Placement = pos=(0,0,0) rot=(1,0,0;1.5708rad)
  Profile = -> Sketch235
  ReferenceAxis = -> Sketch235 [N_Axis]
  Refine = true
  SideType = 0
  Suppressed = false
  Type = 0
  Type2 = 0
FEATURE [PartDesign::Fillet] Fillet011
  Base = -> Pad096 [Edge61]
  BaseFeature = -> Pad096
  Placement = pos=(0,0,0) rot=(1,0,0;1.5708rad)
  Radius = 1
  Refine = true
  SupportTransform = false
  Suppressed = false
  UseAllEdges = false
FEATURE [Sketcher::SketchObject] Sketch245
  ArcFitTolerance = 1e-06
  AttachmentSupport = -> [Fillet011]
  ExternalGeometry = -> [Fillet011]
  ExternalTypes = [0]
  FullyConstrained = true
  MakeInternals = false
  MapMode = 5
  Placement = pos=(10,0,0) rot=(0.707107,0,0.707107;3.14159rad)
  sketch-geometry (5):
    g0: LineSegment StartX=-43.7 StartY=4 StartZ=0 EndX=-43.7 EndY=-4 EndZ=0
    g1: LineSegment StartX=-43.7 StartY=-4 StartZ=0 EndX=-39.5 EndY=-4 EndZ=0
    g2: LineSegment StartX=-39.5 StartY=-4 StartZ=0 EndX=-39.5 EndY=4 EndZ=0
    g3: LineSegment StartX=-39.5 StartY=4 StartZ=0 EndX=-43.7 EndY=4 EndZ=0
    g4: GeomPoint [constr] X=-41.6 Y=0 Z=0
  constraints (13):
    c: Coincident(g0,g1)
    c: Coincident(g1,g2)
    c: Coincident(g2,g3)
    c: Coincident(g3,g0)
    c: Vertical(g0)
    c: Vertical(g2)
    c: Horizontal(g1)
    c: Horizontal(g3)
    c: Symmetric(g2,g0,g4)
    c: PointOnObject(g4,g-1)
    c: Distance(g3,g3) = 4.2
    c: DistanceY(g0,g0) = 8
    c: Distance(g-3,g0) = 3.3
FEATURE [PartDesign::Pad] Pad103
  BaseFeature = -> Fillet011
  Direction = (1,0,-2e-16)
  Length = 5
  Length2 = 10
  Placement = pos=(0,0,0) rot=(1,0,0;1.5708rad)
  Profile = -> Sketch245
  ReferenceAxis = -> Sketch245 [N_Axis]
  Refine = true
  SideType = 0
  Suppressed = false
  TaperAngle = -4
  Type = 0
  Type2 = 0
FEATURE [Sketcher::SketchObject] Sketch246
  ArcFitTolerance = 1e-06
  AttachmentSupport = -> [Pad103]
  ExternalGeometry = -> [Pad103]
  ExternalTypes = [0,0]
  FullyConstrained = true
  MakeInternals = false
  MapMode = 5
  Placement = pos=(15,0,0) rot=(0.707107,0,0.707107;3.14159rad)
  sketch-geometry (4):
    g0: Circle CenterX=-41.6 CenterY=2.30024 CenterZ=0 NormalX=0 NormalY=0 NormalZ=1 AngleXU=0 Radius=1.15012
    g1: Circle CenterX=-41.6 CenterY=-1.38e-14 CenterZ=0 NormalX=0 NormalY=0 NormalZ=1 AngleXU=0 Radius=1.15012
    g2: Circle CenterX=-41.6 CenterY=-2.30024 CenterZ=0 NormalX=0 NormalY=0 NormalZ=1 AngleXU=0 Radius=1.15012
    g3: LineSegment [constr] StartX=-41.6 StartY=2.30024 StartZ=0 EndX=-41.6 EndY=-2.30024 EndZ=0
  constraints (10):
    c: Equal(g2,g1)
    c: Equal(g1,g0)
    c: Tangent(g0,g1)
    c: Tangent(g1,g2)
    c: Coincident(g3,g0)
    c: Coincident(g3,g2)
    c: Vertical(g3)
    c: PointOnObject(g1,g3)
    c: Symmetric(g-4,g-3,g1)
    c: Distance(g0,g-3) = 0.2
FEATURE [PartDesign::Pad] Pad104
  BaseFeature = -> Pad103
  Direction = (1,0,-2e-16)
  Length = 10
  Length2 = 10
  Placement = pos=(0,0,0) rot=(1,0,0;1.5708rad)
  Profile = -> Sketch246
  ReferenceAxis = -> Sketch246 [N_Axis]
  Refine = true
  SideType = 0
  Suppressed = false
  Type = 0
  Type2 = 0
FEATURE [PartDesign::Body] Body041  label="ServoBody001"
  AllowCompound = true
  Group = -> [Sketch086,Pad050,Sketch087,Pocket033,Fillet024,Sketch235,Pad096,Fillet011,Sketch245,Pad103,Sketch246,Pad104]
  Origin = -> Origin062
  Placement = pos=(0,0,-1) rot=(0,0,1;0rad)
  Tip = -> Pad104
FEATURE [App::Point] Origin080  label="Origine"
  Role = Origin
FEATURE [App::Part] Part015  label="MG996"
  Group = -> [Body041,Body043]
  Origin = -> Origin061
  Placement = pos=(0,0,0) rot=(1,0,0;1.5708rad)
FEATURE [App::Link] MG996  label="MG997"
  LinkPlacement = pos=(-14,100,-14) rot=(0.901637,-0.432475,-0.004104;3.4929rad)
  LinkedObject = -> Part015
  Placement = pos=(-14,100,-14) rot=(0.901637,-0.432475,-0.004104;3.4929rad)
FEATURE [App::Link] RoundServoHorn  label="RoundServoHorn001"
  LinkPlacement = pos=(-14.0004,99.9997,-14.0002) rot=(0.111475,0.979708,0.16657;3.0348rad)
  LinkedObject = -> Body042
  Placement = pos=(-14.0004,99.9997,-14.0002) rot=(0.111475,0.979708,0.16657;3.0348rad)
FEATURE [App::Point] Origin148  label="Origine019"
  Role = Origin
FEATURE [App::FeaturePython] GroundedJoint  label="GroundedJoint002"  # Assembly grounded joint (typed FeaturePython)
  ObjectToGround = -> MG996
FEATURE [App::FeaturePython] Joint  label="Revolute009"  # Assembly joint (typed FeaturePython)
  Angle = 0
  AngleMax = 0
  AngleMin = 0
  Detach1 = false
  Detach2 = false
  Distance = 0
  Distance2 = 0
  EnableAngleMax = false
  EnableAngleMin = false
  EnableLengthMax = false
  EnableLengthMin = false
  JointType = 1 (Revolute)
  LengthMax = 0
  LengthMin = 0
  Placement1 = pos=(0,1.42e-14,-2) rot=(0,0,1;0rad)
  Placement2 = pos=(0,0,-2) rot=(0,0,1;0rad)
  Reference1 = -> RoundServoHorn [Edge20,Edge20]
  Reference2 = -> MG996 [Body043.Edge5,Body043.Edge5]
  Suppressed = false
FEATURE [App::FeaturePython] Joint001  label="Fixed008"  # Assembly joint (typed FeaturePython)
  Angle = 0
  AngleMax = 0
  AngleMin = 0
  Detach1 = false
  Detach2 = false
  Distance = 0
  Distance2 = 0
  EnableAngleMax = false
  EnableAngleMin = false
  EnableLengthMax = false
  EnableLengthMin = false
  JointType = 0 (Fixed)
  LengthMax = 0
  LengthMin = 0
  Offset2 = pos=(0,0,0) rot=(0,0,1;0.785398rad)
  Placement2 = pos=(-14,85,-18.5) rot=(0.92388,-0.382683,0;3.14159rad)
  Reference1 = -> RoundServoHorn [Edge24,Edge24]
  Reference2 = -> arm_plate [Edge21,Edge21]
  Suppressed = false
FEATURE [App::FeaturePython] Joint002  label="Fixed009"  # Assembly joint (typed FeaturePython)
  Angle = 0
  AngleMax = 0
  AngleMin = 0
  Detach1 = false
  Detach2 = false
  Distance = 0
  Distance2 = 0
  EnableAngleMax = false
  EnableAngleMin = false
  EnableLengthMax = false
  EnableLengthMin = false
  JointType = 0 (Fixed)
  LengthMax = 0
  LengthMin = 0
  Placement1 = pos=(-12,2.84e-14,-18.5) rot=(-0.707107,-0.707107,0;3.14159rad)
  Placement2 = pos=(-12,0,-18.5) rot=(-0.707107,-0.707107,0;3.14159rad)
  Reference1 = -> SupportBras [Edge57,Edge57]
  Reference2 = -> arm_plate [Edge10,Edge10]
  Suppressed = false
FEATURE [App::FeaturePython] Joint003  label="Fixed010"  # Assembly joint (typed FeaturePython)
  Angle = 0
  AngleMax = 0
  AngleMin = 0
  Detach1 = false
  Detach2 = false
  Distance = 0
  Distance2 = 0
  EnableAngleMax = false
  EnableAngleMin = false
  EnableLengthMax = false
  EnableLengthMin = false
  JointType = 0 (Fixed)
  LengthMax = 0
  LengthMin = 0
  Placement1 = pos=(0,0,0) rot=(-0.57735,-0.57735,-0.57735;4.18879rad)
  Placement2 = pos=(0,0,0) rot=(-0.57735,-0.57735,-0.57735;4.18879rad)
  Reference1 = -> Coulisse [Edge21,Edge21]
  Reference2 = -> SupportBras [Edge67,Edge67]
  Suppressed = false
FEATURE [App::FeaturePython] Joint004  label="Fixed011"  # Assembly joint (typed FeaturePython)
  Angle = 0
  AngleMax = 0
  AngleMin = 0
  Detach1 = false
  Detach2 = false
  Distance = 0
  Distance2 = 0
  EnableAngleMax = false
  EnableAngleMin = false
  EnableLengthMax = false
  EnableLengthMin = false
  JointType = 0 (Fixed)
  LengthMax = 0
  LengthMin = 0
  Placement1 = pos=(-2.84e-14,2.84e-14,4) rot=(0,0,1;0rad)
  Placement2 = pos=(-8,-2.84e-14,2.84e-14) rot=(-0.57735,-0.57735,-0.57735;4.18879rad)
  Reference1 = -> M8_Écrou004 [Edge2,Edge2]
  Reference2 = -> SupportBras [Edge35,Edge35]
  Suppressed = false
FEATURE [App::FeaturePython] Joint005  label="Fixed012"  # Assembly joint (typed FeaturePython)
  Angle = 0
  AngleMax = 0
  AngleMin = 0
  Detach1 = false
  Detach2 = false
  Distance = 0
  Distance2 = 0
  EnableAngleMax = false
  EnableAngleMin = false
  EnableLengthMax = false
  EnableLengthMin = false
  JointType = 0 (Fixed)
  LengthMax = 0
  LengthMin = 0
  Placement1 = pos=(-37.5,1.8e-15,0) rot=(-0.707107,0,0.707107;3.14159rad)
  Placement2 = pos=(0,0,0) rot=(-0.57735,-0.57735,-0.57735;4.18879rad)
  Reference1 = -> Axe [Edge47,Edge47]
  Reference2 = -> ContreRotation [Edge10,Edge10]
  Suppressed = false
FEATURE [App::FeaturePython] Joint006  label="Fixed013"  # Assembly joint (typed FeaturePython)
  Angle = 0
  AngleMax = 0
  AngleMin = 0
  Detach1 = false
  Detach2 = false
  Distance = 0
  Distance2 = 0
  EnableAngleMax = false
  EnableAngleMin = false
  EnableLengthMax = false
  EnableLengthMin = false
  JointType = 0 (Fixed)
  LengthMax = 0
  LengthMin = 0
  Placement2 = pos=(3,0,0) rot=(-0.57735,-0.57735,-0.57735;4.18879rad)
  Reference1 = -> M3x10_Vis [Edge5,Edge5]
  Reference2 = -> ContreRotation [Edge18,Edge18]
  Suppressed = false
FEATURE [App::FeaturePython] Joint007  label="Fixed014"  # Assembly joint (typed FeaturePython)
  Angle = 0
  AngleMax = 0
  AngleMin = 0
  Detach1 = false
  Detach2 = false
  Distance = 0
  Distance2 = 0
  EnableAngleMax = false
  EnableAngleMin = false
  EnableLengthMax = false
  EnableLengthMin = false
  JointType = 0 (Fixed)
  LengthMax = 0
  LengthMin = 0
  Placement1 = pos=(-3.5,-6,-1.6485e-12) rot=(-1,0,0;4.71239rad)
  Placement2 = pos=(0,0,0) rot=(0,-0.707107,-0.707107;3.14159rad)
  Reference1 = -> Axe [Edge30,Edge30]
  Reference2 = -> ConnecteurPneu [Edge17,Edge17]
  Suppressed = false
FEATURE [App::FeaturePython] Joint008  label="Cylindrical015"  # Assembly joint (typed FeaturePython)
  Angle = 0
  AngleMax = 0
  AngleMin = 0
  Detach1 = false
  Detach2 = false
  Distance = 0
  Distance2 = 0
  EnableAngleMax = false
  EnableAngleMin = false
  EnableLengthMax = false
  EnableLengthMin = false
  JointType = 2 (Cylindrical)
  LengthMax = 0
  LengthMin = 0
  Placement1 = pos=(-24.25,-1.8e-15,0) rot=(-0.707107,0,-0.707107;3.14159rad)
  Placement2 = pos=(-4.25,-2.84e-14,-7.1e-15) rot=(-0.57735,-0.57735,-0.57735;4.18879rad)
  Reference1 = -> Axe [Face21,Face21]
  Reference2 = -> Coulisse [Face3,Face3]
  Suppressed = false
FEATURE [Assembly::JointGroup] Joints001
  Group = -> [GroundedJoint,Joint,Joint001,Joint002,Joint003,Joint004,Joint005,Joint006,Joint007,Joint008]
FEATURE [Assembly::AssemblyObject] Assembly001
  Group = -> [Joints001,SupportBras,M8_Écrou004,Coulisse,ConnecteurPneu,Axe,ContreRotation,M3x10_Vis,arm_plate,MG996,RoundServoHorn,GroundedJoint,Joint,Joint001,Joint002,Joint003,Joint004,Joint005,Joint006,Joint007,Joint008]
  Origin = -> Origin
  Placement = pos=(18.2501,-34.1274,-47.5592) rot=(0.341023,0.876017,0.341023;1.70278rad)
  Type = Assembly
FEATURE [App::Point] Origin150  label="Origine021"
  Role = Origin
FEATURE [App::Link] MG997  label="MG998"
  LinkedObject = -> Part015
FEATURE [App::Link] RoundServoHorn001  label="RoundServoHorn002"
  LinkPlacement = pos=(0,0,0) rot=(0,0,1;3.93091rad)
  LinkedObject = -> Body042
  Placement = pos=(0,0,0) rot=(0,0,1;3.93091rad)
FEATURE [App::Link] ConnecteurPneu001  label="ConnecteurPneu002"
  LinkPlacement = pos=(-85.0425,10.6558,-24.5) rot=(0.57886,-0.576594,0.576594;4.19105rad)
  LinkedObject = -> Body002
  Placement = pos=(-85.0425,10.6558,-24.5) rot=(0.57886,-0.576594,0.576594;4.19105rad)
FEATURE [App::Link] Axe001  label="Axe002"
  LinkPlacement = pos=(-85.0562,14.1558,-18.5) rot=(0.57584,0.578104,-0.578104;4.18652rad)
  LinkedObject = -> Body
  Placement = pos=(-85.0562,14.1558,-18.5) rot=(0.57584,0.578104,-0.578104;4.18652rad)
FEATURE [App::Link] ContreRotation001  label="ContreRotation002"
  LinkPlacement = pos=(-84.9091,-23.3439,-18.5) rot=(0.708492,-0.705719,0;3.14159rad)
  LinkedObject = -> Body004
  Placement = pos=(-84.9091,-23.3439,-18.5) rot=(0.708492,-0.705719,0;3.14159rad)
FEATURE [App::Link] M3x10_Vis001  label="M3x10-Vis002"
  LinkPlacement = pos=(-84.8973,-26.3439,-18.5) rot=(-0.001387,0.707106,-0.707106;3.13882rad)
  LinkedObject = -> Screw
  Placement = pos=(-84.8973,-26.3439,-18.5) rot=(-0.001387,0.707106,-0.707106;3.13882rad)
FEATURE [App::Link] M8_Écrou005  label="M8-Écrou006"
  LinkPlacement = pos=(-84.9444,-14.3333,-18.5) rot=(-0.001387,0.707106,-0.707106;3.13882rad)
  LinkedObject = -> Nut001
  Placement = pos=(-84.9444,-14.3333,-18.5) rot=(-0.001387,0.707106,-0.707106;3.13882rad)
FEATURE [App::Link] SupportBras001  label="SupportBras002"
  LinkPlacement = pos=(-84.9444,-14.3333,-18.5) rot=(0.708492,-0.705719,0;3.14159rad)
  LinkedObject = -> Body005
  Placement = pos=(-84.9444,-14.3333,-18.5) rot=(0.708492,-0.705719,0;3.14159rad)
FEATURE [App::Link] Coulisse001  label="Coulisse002"
  LinkPlacement = pos=(-84.9758,-6.33338,-18.5) rot=(0,0,1;1.57472rad)
  LinkedObject = -> Body001
  Placement = pos=(-84.9758,-6.33338,-18.5) rot=(0,0,1;1.57472rad)
FEATURE [App::Link] arm_plate001  label="arm-plate002"
  LinkPlacement = pos=(-84.9444,-14.3333,21.5) rot=(0,0,-1;1.56687rad)
  LinkedObject = -> Body006
  Placement = pos=(-84.9444,-14.3333,21.5) rot=(0,0,-1;1.56687rad)
FEATURE [App::FeaturePython] GroundedJoint001  label="GroundedJoint004"  # Assembly grounded joint (typed FeaturePython)
  ObjectToGround = -> MG997
FEATURE [App::Point] Origin152  label="Origine023"
  Role = Origin
FEATURE [App::Link] MGN9_225mm_Custom  label="MGN9-225mm-Custom001"
  LinkPlacement = pos=(0,0,0) rot=(0,1,0;1.5708rad)
  LinkedObject = -> <external linear-lifter.FCStd>#MGN9_225mm_Custom
  Placement = pos=(0,0,0) rot=(0,1,0;1.5708rad)
FEATURE [App::Link] ClipRail  label="ClipRail001"
  LinkPlacement = pos=(0.499992,-64.9133,133.531) rot=(0.5,0.866025,0;3.14159rad)
  LinkedObject = -> <external linear-lifter.FCStd>#ClipRail
  Placement = pos=(0.499992,-64.9133,133.531) rot=(0.5,0.866025,0;3.14159rad)
FEATURE [App::Link] ClipRail001  label="ClipRail002"
  LinkPlacement = pos=(0.499992,-64.9133,213.531) rot=(0,0,1;1.0472rad)
  LinkedObject = -> <external linear-lifter.FCStd>#ClipRail001
  Placement = pos=(0.499992,-64.9133,213.531) rot=(0,0,1;1.0472rad)
FEATURE [App::Link] ClipRail002  label="ClipRail003"
  LinkPlacement = pos=(0.499992,-64.9133,53.5308) rot=(0.5,0.866025,0;3.14159rad)
  LinkedObject = -> <external linear-lifter.FCStd>#ClipRail002
  Placement = pos=(0.499992,-64.9133,53.5308) rot=(0.5,0.866025,0;3.14159rad)
FEATURE [App::Link] Chariot  label="Chariot001"
  LinkPlacement = pos=(0.499992,-4.91335,67.3673) rot=(0,-1,0;1.5708rad)
  LinkedObject = -> <external linear-lifter.FCStd>#Chariot
  Placement = pos=(0.499992,-4.91335,67.3673) rot=(0,-1,0;1.5708rad)
FEATURE [App::Link] mgn9c  label="mgn9c001"
  LinkPlacement = pos=(0.499992,-12.9133,67.3673) rot=(0,1,0;1.5708rad)
  LinkedObject = -> <external linear-lifter.FCStd>#mgn9c
  Placement = pos=(0.499992,-12.9133,67.3673) rot=(0,1,0;1.5708rad)
FEATURE [App::Link] Body028  label="Body029"
  LinkPlacement = pos=(-31.3959,8.30559,185.591) rot=(-0.157315,-0.090826,0.983363;1.06179rad)
  LinkedObject = -> <external linear-lifter.FCStd>#Body028
  Placement = pos=(-31.3959,8.30559,185.591) rot=(-0.157315,-0.090826,0.983363;1.06179rad)
FEATURE [App::Link] MF001
  LinkPlacement = pos=(-28.0959,14.0214,185.591) rot=(0.092352,0.344662,-0.934173;0.558662rad)
  LinkedObject = -> <external linear-lifter.FCStd>#MF001
  Placement = pos=(-28.0959,14.0214,185.591) rot=(0.092352,0.344662,-0.934173;0.558662rad)
FEATURE [App::Link] MF002
  LinkPlacement = pos=(-31.0959,8.8252,185.591) rot=(0.961552,-0.257647,-0.095058;3.19252rad)
  LinkedObject = -> <external linear-lifter.FCStd>#MF002
  Placement = pos=(-31.0959,8.8252,185.591) rot=(0.961552,-0.257647,-0.095058;3.19252rad)
FEATURE [App::Link] Bielle001  label="Bielle002"
  LinkPlacement = pos=(2.64807,-7.19277,280.131) rot=(0.167978,0.096982,0.981009;1.06388rad)
  LinkedObject = -> <external linear-lifter.FCStd>#Bielle001
  Placement = pos=(2.64807,-7.19277,280.131) rot=(0.167978,0.096982,0.981009;1.06388rad)
FEATURE [App::Link] RoundServoHorn002  label="RoundServoHorn003"
  LinkPlacement = pos=(1.14807,-9.79085,280.131) rot=(0.250983,0.666109,0.702358;2.91122rad)
  LinkedObject = -> <external linear-lifter.FCStd>#RoundServoHorn
  Placement = pos=(1.14807,-9.79085,280.131) rot=(0.250983,0.666109,0.702358;2.91122rad)
FEATURE [App::Link] ServoLifterSpacer  label="ServoLifterSpacer001"
  LinkPlacement = pos=(-2.85193,-16.719,280.131) rot=(0,0,1;1.0472rad)
  LinkedObject = -> <external linear-lifter.FCStd>#ServoLifterSpacer
  Placement = pos=(-2.85193,-16.719,280.131) rot=(0,0,1;1.0472rad)
FEATURE [App::Link] ServoLifterPlate  label="ServoLifterPlate001"
  LinkPlacement = pos=(-2.85193,-16.719,280.131) rot=(0,0,1;1.0472rad)
  LinkedObject = -> <external linear-lifter.FCStd>#ServoLifterPlate
  Placement = pos=(-2.85193,-16.719,280.131) rot=(0,0,1;1.0472rad)
FEATURE [App::Link] Bielle002  label="Bielle003"
  LinkPlacement = pos=(1.14807,-9.79085,280.131) rot=(0.167978,0.096982,0.981009;1.06388rad)
  LinkedObject = -> <external linear-lifter.FCStd>#Bielle002
  Placement = pos=(1.14807,-9.79085,280.131) rot=(0.167978,0.096982,0.981009;1.06388rad)
FEATURE [App::Link] MG998  label="MG999"
  LinkPlacement = pos=(1.14807,-9.79085,280.131) rot=(0.654654,0.377964,0.654654;3.86433rad)
  LinkedObject = -> <external linear-lifter.FCStd>#MG997
  Placement = pos=(1.14807,-9.79085,280.131) rot=(0.654654,0.377964,0.654654;3.86433rad)
FEATURE [Assembly::AssemblyLink] linear_lifter_asm  label="linear-lifter-asm"
  Group = -> [MGN9_225mm_Custom,ClipRail,ClipRail001,ClipRail002,Chariot,mgn9c,Body028,MF001,MF002,Bielle001,RoundServoHorn002,ServoLifterSpacer,ServoLifterPlate,Bielle002,MG998]
  LinkedObject = -> <external linear-lifter.FCStd>#Assembly
  Origin = -> Origin151
  Rigid = true
FEATURE [App::FeaturePython] GroundedJoint002  label="GroundedJoint005"  # Assembly grounded joint (typed FeaturePython)
  ObjectToGround = -> linear_lifter_asm
FEATURE [Assembly::JointGroup] Joints
  Group = -> [GroundedJoint002]
FEATURE [App::Point] Origin154  label="Origine025"
  Role = Origin
FEATURE [PartDesign::SubShapeBinder] Binder
  BindCopyOnChange = 0
  BindMode = 2
  ClaimChildren = false
  Context = -> Assembly [Body044.Binder.]
  Fuse = false
  MakeFace = true
  OffsetFill = false
  OffsetIntersection = false
  OffsetJoinType = 0
  OffsetOpenResult = false
  PartialLoad = false
  Refine = true
  Relative = false
  _Version = 2
FEATURE [Sketcher::SketchObject] Sketch247
  ArcFitTolerance = 1e-06
  AttachmentSupport = -> [Origin153]
  ExternalGeometry = -> [Binder]
  ExternalTypes = [0,0,0,0]
  FullyConstrained = true
  MakeInternals = false
  MapMode = 5
  Placement = pos=(0,0,0) rot=(1,0,0;1.5708rad)
  sketch-geometry (7):
    g0: Circle CenterX=20 CenterY=0 CenterZ=0 NormalX=0 NormalY=0 NormalZ=1 AngleXU=0 Radius=1.7
    g1: Circle CenterX=-16.383 CenterY=11.4715 CenterZ=0 NormalX=0 NormalY=0 NormalZ=1 AngleXU=0 Radius=1.7
    g2: Circle CenterX=-16.383 CenterY=-11.4715 CenterZ=0 NormalX=0 NormalY=0 NormalZ=1 AngleXU=0 Radius=1.7
    g3: LineSegment StartX=24 StartY=-20.75 StartZ=0 EndX=24 EndY=20.75 EndZ=0
    g4: LineSegment StartX=24 StartY=20.75 StartZ=0 EndX=-56 EndY=20.75 EndZ=0
    g5: LineSegment StartX=-56 StartY=20.75 StartZ=0 EndX=-56 EndY=-20.7501 EndZ=0
    g6: LineSegment StartX=-56 StartY=-20.7501 StartZ=0 EndX=24 EndY=-20.75 EndZ=0
  constraints (17):
    c: Coincident(g0,g-3)
    c: Coincident(g1,g-4)
    c: Coincident(g2,g-5)
    c: Equal(g2,g1)
    c: Equal(g1,g0)
    c: Diameter(g0) = 3.4
    c: Coincident(g3,g4)
    c: Horizontal(g4)
    c: Coincident(g4,g5)
    c: Vertical(g5)
    c: Coincident(g5,g6)
    c: Coincident(g6,g3)
    c: Symmetric(g3,g3,g-1)
    c: Equal(g6,g4)
    c: PointOnObject(g-6,g3)
    c: DistanceY(g3,g3) = 41.5
    c: Distance(g3,g5) = 80
FEATURE [PartDesign::Pad] Pad105
  Direction = (0,-1,2e-16)
  Length = 15
  Length2 = 10
  Profile = -> Sketch247
  ReferenceAxis = -> Sketch247 [N_Axis]
  Refine = true
  SideType = 0
  Suppressed = false
  Type = 0
  Type2 = 0
FEATURE [App::Link] servo_support  label="servo-support001"
  LinkPlacement = pos=(0.499992,5.08665,67.3673) rot=(0.707107,0,0.707107;3.14159rad)
  LinkedObject = -> Body044
  Placement = pos=(0.499992,5.08665,67.3673) rot=(0.707107,0,0.707107;3.14159rad)
FEATURE [Sketcher::SketchObject] Sketch248
  ArcFitTolerance = 1e-06
  AttachmentSupport = -> [Pad105]
  ExternalGeometry = -> [Pad105]
  ExternalTypes = [0,0]
  FullyConstrained = true
  MakeInternals = false
  MapMode = 5
  Placement = pos=(0,-15,0) rot=(1,0,0;1.5708rad)
  sketch-geometry (8):
    g0: LineSegment StartX=-56 StartY=-20.7501 StartZ=0 EndX=-47 EndY=-20.7501 EndZ=0
    g1: LineSegment StartX=-47 StartY=-20.7501 StartZ=0 EndX=-47 EndY=-10.7501 EndZ=0
    g2: LineSegment StartX=-47 StartY=-10.7501 StartZ=0 EndX=-56 EndY=-10.7501 EndZ=0
    g3: LineSegment StartX=-56 StartY=-10.7501 StartZ=0 EndX=-56 EndY=-20.7501 EndZ=0
    g4: LineSegment StartX=-7 StartY=-20.75 StartZ=0 EndX=2 EndY=-20.75 EndZ=0
    g5: LineSegment StartX=2 StartY=-20.75 StartZ=0 EndX=2 EndY=-10.75 EndZ=0
    g6: LineSegment StartX=2 StartY=-10.75 StartZ=0 EndX=-7 EndY=-10.75 EndZ=0
    g7: LineSegment StartX=-7 StartY=-10.75 StartZ=0 EndX=-7 EndY=-20.75 EndZ=0
  constraints (23):
    c: Coincident(g0,g1)
    c: Coincident(g1,g2)
    c: Coincident(g2,g3)
    c: Coincident(g3,g0)
    c: Horizontal(g0)
    c: Horizontal(g2)
    c: Vertical(g1)
    c: Vertical(g3)
    c: Coincident(g0,g-3)
    c: Coincident(g4,g5)
    c: Coincident(g5,g6)
    c: Coincident(g6,g7)
    c: Coincident(g7,g4)
    c: Horizontal(g4)
    c: Horizontal(g6)
    c: Vertical(g5)
    c: Vertical(g7)
    c: PointOnObject(g4,g-4)
    c: Distance(g7,g1) = 40
    c: Distance(g5,g3) = 58
    c: Equal(g2,g6)
    c: DistanceY(g3,g3) = 10
    c: Equal(g7,g1)
FEATURE [PartDesign::Pad] Pad106
  BaseFeature = -> Pad105
  Direction = (0,-1,2e-16)
  Length = 20
  Length2 = 10
  Profile = -> Sketch248
  ReferenceAxis = -> Sketch248 [N_Axis]
  Refine = true
  SideType = 0
  Suppressed = false
  Type = 0
  Type2 = 0
FEATURE [PartDesign::Draft] Draft
  Angle = 30
  Base = -> Pad106 [Face15]
  BaseFeature = -> Pad106
  NeutralPlane = -> Pad106 [Face17]
  Refine = true
  Reversed = true
  SupportTransform = false
  Suppressed = false
FEATURE [Sketcher::SketchObject] Sketch249
  ArcFitTolerance = 1e-06
  AttachmentSupport = -> [Draft]
  ExternalGeometry = -> [Draft]
  ExternalTypes = [0,0,0]
  FullyConstrained = true
  MakeInternals = false
  MapMode = 5
  Placement = pos=(0,-4.6e-15,-20.7501) rot=(1,0,0;3.14159rad)
  sketch-geometry (11):
    g0: LineSegment [constr] StartX=-51.5 StartY=30 StartZ=0 EndX=-51.5 EndY=20 EndZ=0
    g1: LineSegment [constr] StartX=-51.5 StartY=20 StartZ=0 EndX=-2.5 EndY=20 EndZ=0
    g2: LineSegment [constr] StartX=-2.5 StartY=20 StartZ=0 EndX=-2.5 EndY=30 EndZ=0
    g3: LineSegment [constr] StartX=-2.5 StartY=30 StartZ=0 EndX=-51.5 EndY=30 EndZ=0
    g4: GeomPoint [constr] X=-27 Y=25 Z=0
    g5: LineSegment [constr] StartX=-27 StartY=30 StartZ=0 EndX=-27 EndY=20 EndZ=0
    g6: LineSegment [constr] StartX=-51.5 StartY=25 StartZ=0 EndX=-2.5 EndY=25 EndZ=0
    g7: Circle CenterX=-51.5 CenterY=30 CenterZ=0 NormalX=0 NormalY=0 NormalZ=1 AngleXU=0 Radius=2.25
    g8: Circle CenterX=-51.5 CenterY=20 CenterZ=0 NormalX=0 NormalY=0 NormalZ=1 AngleXU=0 Radius=2.25
    g9: Circle CenterX=-2.5 CenterY=30 CenterZ=0 NormalX=0 NormalY=0 NormalZ=1 AngleXU=0 Radius=2.25
    g10: Circle CenterX=-2.5 CenterY=20 CenterZ=0 NormalX=0 NormalY=0 NormalZ=1 AngleXU=0 Radius=2.25
  constraints (23):
    c: Coincident(g0,g1)
    c: Coincident(g1,g2)
    c: Coincident(g2,g3)
    c: Coincident(g3,g0)
    c: Vertical(g0)
    c: Horizontal(g1)
    c: DistanceY(g2,g2) = 10
    c: DistanceX(g3,g3) = 49
    c: Symmetric(g0,g2,g4)
    c: Symmetric(g3,g3,g5)
    c: Symmetric(g1,g1,g5)
    c: Symmetric(g-3,g-5,g5)
    c: Symmetric(g0,g0,g6)
    c: Symmetric(g2,g2,g6)
    c: Symmetric(g-3,g-4,g6)
    c: Coincident(g7,g0)
    c: Coincident(g8,g0)
    c: Coincident(g9,g2)
    c: Coincident(g10,g1)
    c: Equal(g10,g9)
    c: Equal(g9,g7)
    c: Equal(g7,g8)
    c: Diameter(g7) = 4.5
FEATURE [PartDesign::Pocket] Pocket034
  BaseFeature = -> Draft
  Direction = (0,0,1)
  Length = 5
  Length2 = 5
  Profile = -> Sketch249
  ReferenceAxis = -> Sketch249 [N_Axis]
  Refine = true
  SideType = 0
  Suppressed = false
  Type = 1
  Type2 = 0
FEATURE [PartDesign::Chamfer] Chamfer030
  Angle = 45
  Base = -> Pocket034 [Edge32,Edge45,Edge44,Edge33,Edge38,Edge37,Edge52,Edge51]
  BaseFeature = -> Pocket034
  ChamferType = 0
  FlipDirection = false
  Refine = true
  Size = 0.4
  Size2 = 1
  SupportTransform = false
  Suppressed = false
  UseAllEdges = false
FEATURE [PartDesign::Mirrored] Mirrored
  BaseFeature = -> Chamfer030
  MirrorPlane = -> Sketch248 [H_Axis]
  Originals = -> [Pad106,Draft,Pocket034,Chamfer030]
  Refine = true
  Suppressed = false
  TransformMode = 0
FEATURE [PartDesign::Chamfer] Chamfer031
  Angle = 45
  Base = -> Mirrored [Edge23,Edge1]
  BaseFeature = -> Mirrored
  ChamferType = 0
  FlipDirection = false
  Refine = true
  Size = 6
  Size2 = 1
  SupportTransform = false
  Suppressed = false
  UseAllEdges = false
FEATURE [Sketcher::SketchObject] Sketch250
  ArcFitTolerance = 1e-06
  AttachmentSupport = -> [Chamfer031]
  ExternalGeometry = -> [Chamfer031]
  ExternalTypes = [0]
  FullyConstrained = true
  MakeInternals = false
  MapMode = 5
  Placement = pos=(-56,0,0) rot=(0.57735,-0.57735,-0.57735;2.0944rad)
  sketch-geometry (5):
    g0: LineSegment StartX=24 StartY=-7 StartZ=0 EndX=24 EndY=7 EndZ=0
    g1: LineSegment StartX=24 StartY=7 StartZ=0 EndX=6 EndY=7 EndZ=0
    g2: LineSegment StartX=6 StartY=7 StartZ=0 EndX=6 EndY=-7 EndZ=0
    g3: LineSegment StartX=6 StartY=-7 StartZ=0 EndX=24 EndY=-7 EndZ=0
    g4: GeomPoint [constr] X=15 Y=8e-16 Z=0
  constraints (12):
    c: Coincident(g0,g1)
    c: Coincident(g1,g2)
    c: Coincident(g2,g3)
    c: Coincident(g3,g0)
    c: Vertical(g0)
    c: Vertical(g2)
    c: Horizontal(g1)
    c: Horizontal(g3)
    c: Symmetric(g2,g0,g4)
    c: Symmetric(g-3,g-3,g4)
    c: Distance(g2,g2) = 14
    c: Distance(g1,g-2) = 6
FEATURE [PartDesign::Pocket] Pocket035
  BaseFeature = -> Chamfer031
  Direction = (1,0,0)
  Length = 60
  Length2 = 5
  Profile = -> Sketch250
  ReferenceAxis = -> Sketch250 [N_Axis]
  Refine = true
  SideType = 0
  Suppressed = false
  Type = 0
  Type2 = 0
FEATURE [PartDesign::Chamfer] Chamfer032
  Angle = 45
  Base = -> Pocket035 [Edge48,Edge47,Edge49]
  BaseFeature = -> Pocket035
  ChamferType = 0
  FlipDirection = false
  Refine = true
  Size = 2
  Size2 = 1
  SupportTransform = false
  Suppressed = false
  UseAllEdges = false
FEATURE [PartDesign::Fillet] Fillet025
  Base = -> Chamfer032 [Edge65]
  BaseFeature = -> Chamfer032
  Radius = 4
  Refine = true
  SupportTransform = false
  Suppressed = false
  UseAllEdges = false
FEATURE [PartDesign::Chamfer] Chamfer033
  Angle = 45
  Base = -> Fillet025 [Edge1,Edge8]
  BaseFeature = -> Fillet025
  ChamferType = 0
  FlipDirection = false
  Refine = true
  Size = 1
  Size2 = 1
  SupportTransform = false
  Suppressed = false
  UseAllEdges = false
FEATURE [PartDesign::Chamfer] Chamfer034
  Angle = 45
  Base = -> Chamfer033 [Edge18,Edge11]
  BaseFeature = -> Chamfer033
  ChamferType = 0
  FlipDirection = false
  Refine = true
  Size = 2
  Size2 = 1
  SupportTransform = false
  Suppressed = false
  UseAllEdges = false
FEATURE [PartDesign::Chamfer] Chamfer035
  Angle = 45
  Base = -> Chamfer034 [Edge65,Edge57]
  BaseFeature = -> Chamfer034
  ChamferType = 0
  FlipDirection = false
  Refine = true
  Size = 2
  Size2 = 1
  SupportTransform = false
  Suppressed = false
  UseAllEdges = false
FEATURE [Sketcher::SketchObject] Sketch251
  ArcFitTolerance = 1e-06
  AttachmentSupport = -> [Chamfer035]
  ExternalGeometry = -> [Chamfer035]
  ExternalTypes = [0,0]
  FullyConstrained = true
  MakeInternals = false
  MapMode = 5
  Placement = pos=(-56,0,0) rot=(0.57735,-0.57735,-0.57735;2.0944rad)
  sketch-geometry (10):
    g0: LineSegment [constr] StartX=7 StartY=20.75 StartZ=0 EndX=15 EndY=30.75 EndZ=0
    g1: LineSegment [constr] StartX=15 StartY=20.75 StartZ=0 EndX=15 EndY=30.75 EndZ=0
    g2: LineSegment StartX=15 StartY=20.75 StartZ=0 EndX=7 EndY=20.75 EndZ=0
    g3: LineSegment StartX=7 StartY=20.75 StartZ=0 EndX=14 EndY=29.5 EndZ=0
    g4: LineSegment StartX=14 StartY=29.5 StartZ=0 EndX=15 EndY=29.5 EndZ=0
    g5: LineSegment StartX=15 StartY=29.5 StartZ=0 EndX=15 EndY=20.75 EndZ=0
    g6: LineSegment StartX=15 StartY=-20.7501 StartZ=0 EndX=15 EndY=-29.5001 EndZ=0
    g7: LineSegment StartX=15 StartY=-29.5001 StartZ=0 EndX=14 EndY=-29.5001 EndZ=0
    g8: LineSegment StartX=7 StartY=-20.7501 StartZ=0 EndX=14 EndY=-29.5001 EndZ=0
    g9: LineSegment StartX=7 StartY=-20.7501 StartZ=0 EndX=15 EndY=-20.7501 EndZ=0
  constraints (27):
    c: PointOnObject(g0,g-3)
    c: Coincident(g1,g-3)
    c: Coincident(g1,g0)
    c: Coincident(g2,g1)
    c: Coincident(g2,g0)
    c: Vertical(g1)
    c: DistanceY(g1,g1) = 10
    c: DistanceX(g2,g2) = 8
    c: Coincident(g3,g0)
    c: PointOnObject(g3,g0)
    c: Coincident(g4,g3)
    c: PointOnObject(g4,g1)
    c: Coincident(g5,g4)
    c: Coincident(g5,g1)
    c: Perpendicular(g5,g4)
    c: Distance(g4,g4) = 1
    c: Coincident(g6,g-4)
    c: Coincident(g7,g6)
    c: PointOnObject(g8,g-4)
    c: Coincident(g8,g7)
    c: Coincident(g9,g8)
    c: Coincident(g9,g6)
    c: Vertical(g6)
    c: Perpendicular(g6,g7)
    c: Equal(g6,g5)
    c: Equal(g3,g8)
    c: Equal(g7,g4)
FEATURE [PartDesign::Pad] Pad107
  BaseFeature = -> Chamfer035
  Direction = (-1,0,0)
  Length = 52
  Length2 = 10
  Profile = -> Sketch251
  ReferenceAxis = -> Sketch251 [N_Axis]
  Refine = true
  Reversed = true
  SideType = 0
  Suppressed = false
  Type = 0
  Type2 = 0
FEATURE [Sketcher::SketchObject] Sketch011
  ArcFitTolerance = 0
  AttachmentSupport = -> [YZ_Plane004]
  ExternalTypes = [0]
  FullyConstrained = true
  MakeInternals = false
  MapMode = 5
  Placement = pos=(0,0,0) rot=(0.57735,0.57735,0.57735;2.0944rad)
  sketch-geometry (5):
    g0: ArcOfCircle CenterX=0 CenterY=0 CenterZ=0 NormalX=0 NormalY=0 NormalZ=1 AngleXU=0 Radius=8 StartAngle=2e-16 EndAngle=3.14159
    g1: LineSegment StartX=-8 StartY=4.01e-14 StartZ=0 EndX=-8 EndY=-8 EndZ=0
    g2: LineSegment StartX=-8 StartY=-8 StartZ=0 EndX=8 EndY=-8 EndZ=0
    g3: LineSegment StartX=8 StartY=-8 StartZ=0 EndX=8 EndY=1.8e-15 EndZ=0
    g4: Circle CenterX=0 CenterY=0 CenterZ=0 NormalX=0 NormalY=0 NormalZ=1 AngleXU=0 Radius=4.15
  constraints (14):
    c: Coincident(g0,g-1)
    c: PointOnObject(g0,g-1)
    c: PointOnObject(g0,g-1)
    c: Coincident(g1,g0)
    c: Coincident(g1,g2)
    c: Horizontal(g2)
    c: Coincident(g2,g3)
    c: Coincident(g3,g0)
    c: Vertical(g3)
    c: Vertical(g1)
    c: Diameter(g0) = 16
    c: DistanceY(g2) = -8
    c: Coincident(g4,g0)
    c: Diameter(g4) = 8.3
FEATURE [PartDesign::Pad] Pad
  Direction = (1,0,0)
  Length = 5
  Length2 = 100
  Placement = pos=(0,0,0) rot=(0.57735,0.57735,0.57735;2.0944rad)
  Profile = -> Sketch011
  Refine = true
  Reversed = true
  SideType = 0
  Suppressed = false
  Type = 0
  Type2 = 0
FEATURE [Sketcher::SketchObject] Sketch012
  ArcFitTolerance = 0
  AttachmentSupport = -> [Pad]
  ExternalTypes = [0]
  FullyConstrained = true
  MakeInternals = false
  MapMode = 5
  Placement = pos=(0,-1.8e-15,-8) rot=(0.707107,0.707107,0;3.14159rad)
  sketch-geometry (16):
    g0: LineSegment StartX=-8 StartY=-26 StartZ=0 EndX=8 EndY=-26 EndZ=0
    g1: Circle [constr] CenterX=0 CenterY=-12 CenterZ=0 NormalX=0 NormalY=0 NormalZ=1 AngleXU=0 Radius=10
    g2: LineSegment StartX=-8 StartY=0 StartZ=0 EndX=8 EndY=0 EndZ=0
    g3: LineSegment StartX=-8 StartY=0 StartZ=0 EndX=-8 EndY=-3.05573 EndZ=0
    g4: LineSegment StartX=8 StartY=0 StartZ=0 EndX=8 EndY=-3.05573 EndZ=0
    g5: LineSegment StartX=8 StartY=-26 StartZ=0 EndX=8 EndY=-20.9443 EndZ=0
    g6: LineSegment StartX=-8 StartY=-26 StartZ=0 EndX=-8 EndY=-20.9443 EndZ=0
    g7: ArcOfCircle CenterX=0 CenterY=-12 CenterZ=0 NormalX=0 NormalY=0 NormalZ=1 AngleXU=0 Radius=12 StartAngle=2.30052 EndAngle=3.98266
    g8: ArcOfCircle CenterX=0 CenterY=-12 CenterZ=0 NormalX=0 NormalY=0 NormalZ=1 AngleXU=0 Radius=12 StartAngle=5.44212 EndAngle=7.12425
    g9: Circle CenterX=-7 CenterY=-12 CenterZ=0 NormalX=0 NormalY=0 NormalZ=1 AngleXU=0 Radius=1.6
    g10: Circle CenterX=7 CenterY=-12 CenterZ=0 NormalX=0 NormalY=0 NormalZ=1 AngleXU=0 Radius=1.6
    g11: Circle CenterX=0 CenterY=-19 CenterZ=0 NormalX=0 NormalY=0 NormalZ=1 AngleXU=0 Radius=1.6
    g12: Circle [constr] CenterX=0 CenterY=-5 CenterZ=0 NormalX=0 NormalY=0 NormalZ=1 AngleXU=0 Radius=1.6
    g13: Circle [constr] CenterX=0 CenterY=-12 CenterZ=0 NormalX=0 NormalY=0 NormalZ=1 AngleXU=0 Radius=7
    g14: LineSegment [constr] StartX=-7 StartY=-12 StartZ=0 EndX=7 EndY=-12 EndZ=0
    g15: Circle CenterX=0 CenterY=-12 CenterZ=0 NormalX=0 NormalY=0 NormalZ=1 AngleXU=0 Radius=1.6
  constraints (43):
    c: Symmetric(g0,g0,g-2)
    c: DistanceY(g0,g-1) = 26
    c: PointOnObject(g1,g-2)
    c: DistanceY(g1,g-1) = 12
    c: Diameter(g1) = 20
    c: PointOnObject(g2,g-1)
    c: Equal(g0,g2)
    c: Symmetric(g2,g2,g-2)
    c: Coincident(g2,g3)
    c: Vertical(g3)
    c: Coincident(g2,g4)
    c: Vertical(g4)
    c: Coincident(g0,g5)
    c: Vertical(g5)
    c: Coincident(g0,g6)
    c: Vertical(g6)
    c: Coincident(g7,g1)
    c: Coincident(g7,g3)
    c: Coincident(g7,g6)
    c: Coincident(g8,g7)
    c: Coincident(g8,g4)
    c: Coincident(g8,g5)
    c: DistanceX(g2,g2) = 16
    c: Diameter(g8) = 24
    c: PointOnObject(g11,g-2)
    c: PointOnObject(g12,g-2)
    c: Coincident(g13,g7)
    c: PointOnObject(g12,g13)
    c: PointOnObject(g10,g13)
    c: PointOnObject(g11,g13)
    c: PointOnObject(g9,g13)
    c: Diameter(g13) = 14
    c: Diameter(g12) = 3.2
    c: Equal(g12,g11)
    c: Equal(g12,g10)
    c: Equal(g12,g9)
    c: Coincident(g14,g9)
    c: Coincident(g14,g10)
    c: Horizontal(g14)
    c: PointOnObject(g7,g14)
    c: Equal(g3,g4)
    c: Coincident(g15,g7)
    c: Equal(g15,g10)
FEATURE [PartDesign::Pad] Pad001
  BaseFeature = -> Pad
  Direction = (0,0,-1)
  Length = 5
  Length2 = 100
  Placement = pos=(0,0,0) rot=(0.57735,0.57735,0.57735;2.0944rad)
  Profile = -> Sketch012
  Refine = true
  SideType = 0
  Suppressed = false
  Type = 0
  Type2 = 0
FEATURE [PartDesign::Chamfer] Chamfer003
  Angle = 45
  Base = -> Pad001 [Edge19,Edge16,Edge17,Edge18]
  BaseFeature = -> Pad001
  ChamferType = 0
  FlipDirection = false
  Placement = pos=(0,0,0) rot=(0.57735,0.57735,0.57735;2.0944rad)
  Refine = true
  Size = 1.8
  Size2 = 1
  SupportTransform = false
  Suppressed = false
  UseAllEdges = false
FEATURE [PartDesign::Fillet] Fillet
  Base = -> Chamfer003 [Edge20,Edge18,Edge22,Edge24,Edge16,Edge15]
  BaseFeature = -> Chamfer003
  Placement = pos=(0,0,0) rot=(0.57735,0.57735,0.57735;2.0944rad)
  Radius = 3
  Refine = true
  SupportTransform = false
  Suppressed = false
  UseAllEdges = false
FEATURE [App::Point] Origin134  label="Origine002"
  Role = Origin
FEATURE [PartDesign::Body] Body003  label="SupportPalonnier"
  AllowCompound = true
  Group = -> [Sketch011,Pad,Sketch012,Pad001,Chamfer003,Fillet]
  Origin = -> Origin005
  Tip = -> Fillet
FEATURE [PartDesign::Draft] Draft001
  Angle = 50
  Base = -> Pad107 [Face76]
  BaseFeature = -> Pad107
  NeutralPlane = -> Pad107 [Face77]
  Refine = true
  Reversed = true
  SupportTransform = false
  Suppressed = false
FEATURE [PartDesign::Draft] Draft002
  Angle = 50
  Base = -> Draft001 [Face82]
  BaseFeature = -> Draft001
  NeutralPlane = -> Draft001 [Face83]
  Refine = true
  Reversed = true
  SupportTransform = false
  Suppressed = false
FEATURE [PartDesign::Fillet] Fillet026
  Base = -> Draft002 [Edge202,Edge192]
  BaseFeature = -> Draft002
  Radius = 5
  Refine = true
  SupportTransform = false
  Suppressed = false
  UseAllEdges = false
FEATURE [Sketcher::SketchObject] Sketch252
  ArcFitTolerance = 1e-06
  AttachmentSupport = -> [Fillet026]
  ExternalGeometry = -> [Fillet026]
  ExternalTypes = [0,0]
  FullyConstrained = true
  MakeInternals = false
  MapMode = 5
  Placement = pos=(-56,0,0) rot=(0.57735,-0.57735,-0.57735;2.0944rad)
  sketch-geometry (10):
    g0: LineSegment StartX=23.5 StartY=23.7501 StartZ=0 EndX=23.5 EndY=17.7501 EndZ=0
    g1: LineSegment StartX=23.5 StartY=17.7501 StartZ=0 EndX=26.5 EndY=17.7501 EndZ=0
    g2: LineSegment StartX=26.5 StartY=17.7501 StartZ=0 EndX=26.5 EndY=23.7501 EndZ=0
    g3: LineSegment StartX=26.5 StartY=23.7501 StartZ=0 EndX=23.5 EndY=23.7501 EndZ=0
    g4: GeomPoint [constr] X=25 Y=20.7501 Z=0
    g5: LineSegment StartX=23.5 StartY=-17.7501 StartZ=0 EndX=23.5 EndY=-23.7501 EndZ=0
    g6: LineSegment StartX=23.5 StartY=-23.7501 StartZ=0 EndX=26.5 EndY=-23.7501 EndZ=0
    g7: LineSegment StartX=26.5 StartY=-23.7501 StartZ=0 EndX=26.5 EndY=-17.7501 EndZ=0
    g8: LineSegment StartX=26.5 StartY=-17.7501 StartZ=0 EndX=23.5 EndY=-17.7501 EndZ=0
    g9: GeomPoint [constr] X=25 Y=-20.7501 Z=0
  constraints (24):
    c: Coincident(g0,g1)
    c: Coincident(g1,g2)
    c: Coincident(g2,g3)
    c: Coincident(g3,g0)
    c: Vertical(g0)
    c: Vertical(g2)
    c: Horizontal(g1)
    c: Horizontal(g3)
    c: Symmetric(g2,g0,g4)
    c: Symmetric(g-4,g-3,g4)
    c: Distance(g3,g3) = 3
    c: Distance(g1,g-4) = 3
    c: Coincident(g5,g6)
    c: Coincident(g6,g7)
    c: Coincident(g7,g8)
    c: Coincident(g8,g5)
    c: Vertical(g5)
    c: Vertical(g7)
    c: Horizontal(g6)
    c: Horizontal(g8)
    c: Symmetric(g7,g5,g9)
    c: Equal(g2,g7)
    c: Equal(g8,g1)
    c: Symmetric(g9,g4,g-1)
FEATURE [PartDesign::Pocket] Pocket036
  BaseFeature = -> Fillet026
  Direction = (1,0,0)
  Length = 5
  Length2 = 5
  Profile = -> Sketch252
  ReferenceAxis = -> Sketch252 [N_Axis]
  Refine = true
  SideType = 0
  Suppressed = false
  Type = 1
  Type2 = 0
FEATURE [Sketcher::SketchObject] Sketch253
  ArcFitTolerance = 1e-06
  AttachmentSupport = -> [Pocket036]
  ExternalGeometry = -> [Binder]
  ExternalTypes = [0,0]
  FullyConstrained = true
  MakeInternals = false
  MapMode = 5
  Placement = pos=(0,0,0) rot=(0,0.707107,0.707107;3.14159rad)
  sketch-geometry (2):
    g0: Circle CenterX=-15 CenterY=-11.547 CenterZ=0 NormalX=0 NormalY=0 NormalZ=1 AngleXU=0 Radius=3.5
    g1: Circle [constr] CenterX=-15 CenterY=11.547 CenterZ=0 NormalX=0 NormalY=0 NormalZ=1 AngleXU=0 Radius=3.55023
  constraints (5):
    c: PointOnObject(g-3,g1)
    c: PointOnObject(g-4,g1)
    c: PointOnObject(g-4,g1)
    c: Symmetric(g0,g1,g-1)
    c: Diameter(g0) = 7
FEATURE [PartDesign::Pocket] Pocket037
  BaseFeature = -> Pocket036
  Direction = (0,-1,0)
  Length = 4
  Length2 = 5
  Profile = -> Sketch253
  ReferenceAxis = -> Sketch253 [N_Axis]
  Refine = true
  SideType = 0
  Suppressed = false
  Type = 0
  Type2 = 0
FEATURE [Sketcher::SketchObject] Sketch254
  ArcFitTolerance = 1e-06
  AttachmentSupport = -> [Origin153]
  ExternalGeometry = -> [Pocket037]
  ExternalTypes = [0]
  FullyConstrained = true
  MakeInternals = false
  MapMode = 5
  sketch-geometry (4):
    g0: LineSegment StartX=24 StartY=-3 StartZ=0 EndX=46.2163 EndY=-8.95284 EndZ=0
    g1: LineSegment StartX=46.2163 StartY=-8.95284 StartZ=0 EndX=46.2163 EndY=0 EndZ=0
    g2: LineSegment StartX=24 StartY=-3 StartZ=0 EndX=24 EndY=-4e-16 EndZ=0
    g3: LineSegment StartX=46.2163 StartY=0 StartZ=0 EndX=24 EndY=-4e-16 EndZ=0
  constraints (11):
    c: PointOnObject(g0,g-3)
    c: Coincident(g1,g0)
    c: PointOnObject(g1,g-1)
    c: Vertical(g1)
    c: Distance(g0,g0) = 23
    c: Coincident(g2,g0)
    c: Coincident(g2,g-3)
    c: Coincident(g3,g1)
    c: Coincident(g3,g2)
    c: Distance(g2,g2) = 3
    c: Angle(g0,g3) = 0.261799
FEATURE [PartDesign::Pad] Pad108
  BaseFeature = -> Pocket037
  Direction = (0,0,1)
  Length = 13
  Length2 = 10
  Profile = -> Sketch254
  ReferenceAxis = -> Sketch254 [N_Axis]
  Refine = true
  SideType = 2
  Suppressed = false
  Type = 0
  Type2 = 0
FEATURE [Sketcher::SketchObject] Sketch255
  ArcFitTolerance = 1e-06
  AttachmentSupport = -> [Pad108]
  ExternalGeometry = -> [Pad108]
  ExternalTypes = [0,0]
  FullyConstrained = true
  MakeInternals = false
  MapMode = 5
  Placement = pos=(46.2163,0,0) rot=(0.57735,0.57735,0.57735;2.0944rad)
  sketch-geometry (8):
    g0: LineSegment StartX=0 StartY=6.5 StartZ=0 EndX=0 EndY=9.5 EndZ=0
    g1: LineSegment StartX=0 StartY=9.5 StartZ=0 EndX=-8.95284 EndY=9.5 EndZ=0
    g2: LineSegment StartX=-8.95284 StartY=9.5 StartZ=0 EndX=-8.95284 EndY=6.5 EndZ=0
    g3: LineSegment StartX=-8.95284 StartY=6.5 StartZ=0 EndX=0 EndY=6.5 EndZ=0
    g4: LineSegment StartX=-8.95284 StartY=-6.5 StartZ=0 EndX=-8.95284 EndY=-9.5 EndZ=0
    g5: LineSegment StartX=-8.95284 StartY=-9.5 StartZ=0 EndX=0 EndY=-9.5 EndZ=0
    g6: LineSegment StartX=0 StartY=-9.5 StartZ=0 EndX=0 EndY=-6.5 EndZ=0
    g7: LineSegment StartX=0 StartY=-6.5 StartZ=0 EndX=-8.95284 EndY=-6.5 EndZ=0
  constraints (21):
    c: Coincident(g0,g1)
    c: Coincident(g1,g2)
    c: Coincident(g2,g3)
    c: Coincident(g3,g0)
    c: Vertical(g0)
    c: Vertical(g2)
    c: Horizontal(g1)
    c: Coincident(g0,g-3)
    c: Coincident(g2,g-3)
    c: Coincident(g4,g5)
    c: Coincident(g5,g6)
    c: Coincident(g6,g7)
    c: Coincident(g7,g4)
    c: Vertical(g4)
    c: Vertical(g6)
    c: Horizontal(g5)
    c: Horizontal(g7)
    c: Coincident(g4,g-4)
    c: PointOnObject(g5,g-2)
    c: Equal(g2,g4)
    c: Distance(g0,g0) = 3
FEATURE [PartDesign::Pad] Pad109
  BaseFeature = -> Pad108
  Direction = (1,0,0)
  Length = 23
  Length2 = 10
  Profile = -> Sketch255
  ReferenceAxis = -> Sketch255 [N_Axis]
  Refine = true
  Reversed = true
  SideType = 0
  Suppressed = false
  Type = 0
  Type2 = 0
FEATURE [PartDesign::Draft] Draft003
  Angle = 10
  Base = -> Pad109 [Face64]
  BaseFeature = -> Pad109
  NeutralPlane = -> Pad109 [Face105]
  Refine = true
  SupportTransform = false
  Suppressed = false
FEATURE [PartDesign::Draft] Draft004
  Angle = 10
  Base = -> Draft003 [Face70]
  BaseFeature = -> Draft003
  NeutralPlane = -> Draft003 [Face105]
  Refine = true
  SupportTransform = false
  Suppressed = false
FEATURE [PartDesign::Fillet] Fillet027
  Base = -> Draft004 [Edge229,Edge218]
  BaseFeature = -> Draft004
  Radius = 2
  Refine = true
  SupportTransform = false
  Suppressed = false
  UseAllEdges = false
FEATURE [Sketcher::SketchObject] Sketch256
  ArcFitTolerance = 1e-06
  AttachmentSupport = -> [Fillet027]
  ExternalGeometry = -> [Fillet027]
  ExternalTypes = [0]
  FullyConstrained = true
  MakeInternals = false
  MapMode = 5
  Placement = pos=(0.857695,3.20096,0) rot=(0.983106,-0.129428,-0.129428;1.58783rad)
  sketch-geometry (1):
    g0: Circle CenterX=36.9587 CenterY=0 CenterZ=0 NormalX=0 NormalY=0 NormalZ=1 AngleXU=0 Radius=2.25
  constraints (3):
    c: PointOnObject(g0,g-1)
    c: Diameter(g0) = 4.5
    c: Distance(g0,g-3) = 13
FEATURE [PartDesign::Pocket] Pocket038
  BaseFeature = -> Fillet027
  Direction = (0.258819,0.965926,0)
  Length = 8
  Length2 = 5
  Profile = -> Sketch256
  ReferenceAxis = -> Sketch256 [N_Axis]
  Refine = true
  SideType = 0
  Suppressed = false
  Type = 0
  Type2 = 0
FEATURE [PartDesign::Fillet] Fillet028
  Base = -> Pocket038 [Edge38]
  BaseFeature = -> Pocket038
  Radius = 2
  Refine = true
  SupportTransform = false
  Suppressed = false
  UseAllEdges = false
FEATURE [PartDesign::Chamfer] Chamfer036
  Angle = 45
  Base = -> Fillet028 [Edge43,Edge37]
  BaseFeature = -> Fillet028
  ChamferType = 0
  FlipDirection = false
  Refine = true
  Size = 0.6
  Size2 = 1
  SupportTransform = false
  Suppressed = false
  UseAllEdges = false
FEATURE [PartDesign::Body] Body044  label="servo-support"
  AllowCompound = true
  Group = -> [Binder,Sketch247,Pad105,Sketch248,Pad106,Draft,Sketch249,Pocket034,Chamfer030,Mirrored,Chamfer031,Sketch250,Pocket035,Chamfer032,Fillet025,Chamfer033,Chamfer034,Chamfer035,Sketch251,Pad107,Draft001,Draft002,Fillet026,Sketch252,Pocket036,Sketch253,Pocket037,Sketch254,Pad108,Sketch255,Pad109,Draft003,Draft004,Fillet027,Sketch256,Pocket038,Fillet028,Chamfer036]
  Origin = -> Origin153
  Placement = pos=(-106,0,0) rot=(0,0,1;0rad)
  Tip = -> Chamfer036
FEATURE [TechDraw::DrawSVGTemplate] Template  label="Modèle"
  Height = 210
  Orientation = 1
  Template = <path>
  Width = 297
FEATURE [Sketcher::SketchObject] Sketch257
  ArcFitTolerance = 1e-06
  AttachmentSupport = -> [Fillet003]
  ExternalGeometry = -> [Fillet003]
  ExternalTypes = [0,0,0]
  FullyConstrained = true
  MakeInternals = false
  MapMode = 5
  Placement = pos=(3.5e-15,-1.2e-15,-21.5) rot=(1,0,0;3.14159rad)
  sketch-geometry (5):
    g0: ArcOfCircle CenterX=-12 CenterY=1e-16 CenterZ=0 NormalX=0 NormalY=0 NormalZ=1 AngleXU=0 Radius=12 StartAngle=5.54333 EndAngle=7.1064
    g1: LineSegment StartX=-3.84157 StartY=-8.8 StartZ=0 EndX=18 EndY=-8.8 EndZ=0
    g2: LineSegment StartX=18 StartY=-8.8 StartZ=0 EndX=18 EndY=8.8 EndZ=0
    g3: LineSegment StartX=18 StartY=8.8 StartZ=0 EndX=-3.84157 EndY=8.8 EndZ=0
    g4: LineSegment StartX=-3.84157 StartY=-8.8 StartZ=0 EndX=-3.1372 EndY=-8.09017 EndZ=0
  constraints (13):
    c: Coincident(g0,g-3)
    c: Coincident(g0,g-3)
    c: Coincident(g1,g-4)
    c: Horizontal(g1)
    c: Coincident(g2,g1)
    c: Vertical(g2)
    c: Coincident(g3,g2)
    c: Coincident(g3,g0)
    c: Horizontal(g3)
    c: PointOnObject(g-5,g2)
    c: Coincident(g4,g1)
    c: Coincident(g4,g0)
    c: Distance(g4,g4) = 1
FEATURE [PartDesign::Pocket] Pocket039
  BaseFeature = -> Fillet003
  Direction = (0,0,1)
  Length = 5
  Length2 = 5
  Placement = pos=(3.5e-15,-1.2e-15,-10.5) rot=(0,0,1;0rad)
  Profile = -> Sketch257
  ReferenceAxis = -> Sketch257 [N_Axis]
  Refine = true
  SideType = 0
  Suppressed = false
  Type = 0
  Type2 = 0
FEATURE [Sketcher::SketchObject] Sketch258
  ArcFitTolerance = 1e-06
  AttachmentSupport = -> [Fillet002]
  ExternalGeometry = -> [Fillet002]
  ExternalTypes = [0,0,0]
  FullyConstrained = true
  MakeInternals = false
  MapMode = 5
  Placement = pos=(0,0,-18.5) rot=(0.707107,0.707107,0;3.14159rad)
  sketch-geometry (5):
    g0: ArcOfCircle CenterX=-5e-15 CenterY=-12 CenterZ=0 NormalX=0 NormalY=0 NormalZ=1 AngleXU=0 Radius=12 StartAngle=0.747584 EndAngle=2.39401
    g1: LineSegment [constr] StartX=-8.8 StartY=-3.84157 StartZ=0 EndX=8.8 EndY=-3.84157 EndZ=0
    g2: LineSegment StartX=8.8 StartY=-3.84157 StartZ=0 EndX=8.8 EndY=18 EndZ=0
    g3: LineSegment StartX=8.8 StartY=18 StartZ=0 EndX=-8.8 EndY=18 EndZ=0
    g4: LineSegment StartX=-8.8 StartY=18 StartZ=0 EndX=-8.8 EndY=-3.84157 EndZ=0
  constraints (13):
    c: Coincident(g0,g-3)
    c: Coincident(g0,g-4)
    c: PointOnObject(g-1,g0)
    c: Coincident(g1,g2)
    c: Coincident(g2,g3)
    c: Coincident(g3,g4)
    c: Coincident(g4,g1)
    c: Horizontal(g3)
    c: Vertical(g2)
    c: Vertical(g4)
    c: Coincident(g1,g0)
    c: Coincident(g1,g0)
    c: PointOnObject(g-5,g3)
FEATURE [PartDesign::Pocket] Pocket040
  BaseFeature = -> Fillet002
  Direction = (0,0,1)
  Length = 7.5
  Length2 = 5
  Placement = pos=(0,0,0) rot=(0.57735,0.57735,0.57735;2.0944rad)
  Profile = -> Sketch258
  ReferenceAxis = -> Sketch258 [N_Axis]
  Refine = true
  SideType = 0
  Suppressed = false
  Type = 0
  Type2 = 0
FEATURE [PartDesign::Body] Body005  label="SupportBras"
  AllowCompound = true
  Group = -> [Sketch014,Pad003,Sketch015,Pad004,Chamfer004,Fillet002,Sketch258,Pocket040]
  Origin = -> Origin139
  Tip = -> Pocket040
FEATURE [TechDraw::DrawProjGroupItem] View
  CoarseView = false
  Direction = (0,0,-1)
  Focus = 100
  HardHidden = false
  IsoCount = 0
  IsoHidden = false
  IsoVisible = false
  LockPosition = false
  Perspective = false
  Rotation = 0
  RotationVector = (1,0,0)
  ScaleType = 0
  ScrubCount = 1
  SeamHidden = false
  SeamVisible = false
  SmoothHidden = false
  SmoothVisible = true
  Source = -> [Pocket039]
  Type = 0
  X = 55.7673
  XDirection = (1e-16,1,0)
  Y = 195.371
FEATURE [App::FeaturePython] Joint009  label="Fixed"  # Assembly joint (typed FeaturePython)
  Angle = 0
  AngleMax = 0
  AngleMin = 0
  Detach1 = false
  Detach2 = false
  Distance = 0
  Distance2 = 0
  EnableAngleMax = false
  EnableAngleMin = false
  EnableLengthMax = false
  EnableLengthMin = false
  JointType = 0 (Fixed)
  LengthMax = 0
  LengthMin = 0
  Offset2 = pos=(0,0,0) rot=(0,0,1;0.785398rad)
  Placement1 = pos=(-14,85,-21.5) rot=(1,0,0;3.14159rad)
  Placement2 = pos=(0,0,0) rot=(0,0,1;0.785398rad)
  Reference1 = -> arm_plate001 [Edge42,Edge42]
  Reference2 = -> RoundServoHorn001 [Edge24,Edge24]
  Suppressed = false
FEATURE [App::FeaturePython] Joint010  label="Revolute015"  # Assembly joint (typed FeaturePython)
  Angle = 0
  AngleMax = 0
  AngleMin = 0
  Detach1 = false
  Detach2 = false
  Distance = 0
  Distance2 = 0
  EnableAngleMax = false
  EnableAngleMin = false
  EnableLengthMax = false
  EnableLengthMin = false
  JointType = 1 (Revolute)
  LengthMax = 0
  LengthMin = 0
  Placement1 = pos=(0,0,-2) rot=(0,0,1;0rad)
  Placement2 = pos=(0,0,-2) rot=(0,0,1;0rad)
  Reference1 = -> RoundServoHorn001 [Edge20,Edge20]
  Reference2 = -> MG997 [Body043.Edge5,Body043.Edge5]
  Suppressed = false
FEATURE [App::FeaturePython] Joint011  label="Fixed015"  # Assembly joint (typed FeaturePython)
  Angle = 0
  AngleMax = 0
  AngleMin = 0
  Detach1 = false
  Detach2 = false
  Distance = 0
  Distance2 = 0
  EnableAngleMax = false
  EnableAngleMin = false
  EnableLengthMax = false
  EnableLengthMin = false
  JointType = 0 (Fixed)
  LengthMax = 0
  LengthMin = 0
  Offset2 = pos=(0,0,0) rot=(0,0,1;1.5708rad)
  Placement1 = pos=(-12,-7,-18.5) rot=(-0.707107,-0.707107,0;3.14159rad)
  Placement2 = pos=(-12,7,-21.5) rot=(0.707107,-0.707107,0;3.14159rad)
  Reference1 = -> SupportBras001 [Edge59,Edge59]
  Reference2 = -> arm_plate001 [Edge38,Edge38]
  Suppressed = false
FEATURE [App::FeaturePython] Joint012  label="Fixed016"  # Assembly joint (typed FeaturePython)
  Angle = 0
  AngleMax = 0
  AngleMin = 0
  Detach1 = false
  Detach2 = false
  Distance = 0
  Distance2 = 0
  EnableAngleMax = false
  EnableAngleMin = false
  EnableLengthMax = false
  EnableLengthMin = false
  JointType = 0 (Fixed)
  LengthMax = 0
  LengthMin = 0
  Placement1 = pos=(0,0,0) rot=(0.57735,0.57735,0.57735;2.0944rad)
  Placement2 = pos=(-8,0,3.6e-15) rot=(-0.57735,-0.57735,-0.57735;4.18879rad)
  Reference1 = -> Coulisse001 [Edge21,Edge21]
  Reference2 = -> SupportBras001 [Edge35,Edge35]
  Suppressed = false
FEATURE [App::FeaturePython] Joint013  label="Fixed017"  # Assembly joint (typed FeaturePython)
  Angle = 0
  AngleMax = 0
  AngleMin = 0
  Detach1 = false
  Detach2 = false
  Distance = 0
  Distance2 = 0
  EnableAngleMax = false
  EnableAngleMin = false
  EnableLengthMax = false
  EnableLengthMin = false
  JointType = 0 (Fixed)
  LengthMax = 0
  LengthMin = 0
  Placement2 = pos=(0,0,0) rot=(-0.57735,-0.57735,-0.57735;4.18879rad)
  Reference1 = -> M8_Écrou005 [Edge27,Edge27]
  Reference2 = -> SupportBras001 [Edge67,Edge67]
  Suppressed = false
FEATURE [App::FeaturePython] Joint014  label="Slider018"  # Assembly joint (typed FeaturePython)
  Angle = 0
  AngleMax = 0
  AngleMin = 0
  Detach1 = false
  Detach2 = false
  Distance = 0
  Distance2 = 0
  EnableAngleMax = false
  EnableAngleMin = false
  EnableLengthMax = false
  EnableLengthMin = false
  JointType = 3 (Slider)
  LengthMax = 0
  LengthMin = 0
  Placement1 = pos=(-37.5,3.6e-15,1.42e-14) rot=(-0.707107,0,-0.707107;3.14159rad)
  Placement2 = pos=(3.5,0,0) rot=(0.57735,0.57735,0.57735;2.0944rad)
  Reference1 = -> Axe001 [Face21,Edge1]
  Reference2 = -> Coulisse001 [Edge5,Edge5]
  Suppressed = false
FEATURE [App::FeaturePython] Joint015  label="Fixed018"  # Assembly joint (typed FeaturePython)
  Angle = 0
  AngleMax = 0
  AngleMin = 0
  Detach1 = false
  Detach2 = false
  Distance = 0
  Distance2 = 0
  EnableAngleMax = false
  EnableAngleMin = false
  EnableLengthMax = false
  EnableLengthMin = false
  JointType = 0 (Fixed)
  LengthMax = 0
  LengthMin = 0
  Offset2 = pos=(0,0,0) rot=(0,0,1;3.14159rad)
  Placement1 = pos=(0,0,0) rot=(0.57735,0.57735,0.57735;2.0944rad)
  Placement2 = pos=(-37.5,3.6e-15,1.42e-14) rot=(0,1,0;4.71239rad)
  Reference1 = -> ContreRotation001 [Edge10,Edge10]
  Reference2 = -> Axe001 [Edge47,Edge47]
  Suppressed = false
FEATURE [App::FeaturePython] Joint016  label="Fixed019"  # Assembly joint (typed FeaturePython)
  Angle = 0
  AngleMax = 0
  AngleMin = 0
  Detach1 = false
  Detach2 = false
  Distance = 0
  Distance2 = 0
  EnableAngleMax = false
  EnableAngleMin = false
  EnableLengthMax = false
  EnableLengthMin = false
  JointType = 0 (Fixed)
  LengthMax = 0
  LengthMin = 0
  Placement2 = pos=(3,0,-3.6e-15) rot=(0.57735,0.57735,0.57735;2.0944rad)
  Reference1 = -> M3x10_Vis001 [Edge5,Edge5]
  Reference2 = -> ContreRotation001 [Edge18,Edge18]
  Suppressed = false
FEATURE [App::FeaturePython] Joint017  label="Fixed020"  # Assembly joint (typed FeaturePython)
  Angle = 0
  AngleMax = 0
  AngleMin = 0
  Detach1 = false
  Detach2 = false
  Distance = 0
  Distance2 = 0
  EnableAngleMax = false
  EnableAngleMin = false
  EnableLengthMax = false
  EnableLengthMin = false
  JointType = 0 (Fixed)
  LengthMax = 0
  LengthMin = 0
  Placement1 = pos=(0,0,0) rot=(0,0.707107,0.707107;3.14159rad)
  Placement2 = pos=(-3.5,6,7.958e-13) rot=(-1,0,0;4.71239rad)
  Reference1 = -> ConnecteurPneu001 [Edge17,Edge17]
  Reference2 = -> Axe001 [Edge1,Edge1]
  Suppressed = false
FEATURE [App::Link] Link  label="Color_Sensor"
  LinkPlacement = pos=(0,0,0.8) rot=(0,0,1;0rad)
  LinkedObject = -> <external ../../ECAD/color-sensor-2026/color-sensor-asm.FCStd>#Part001
  Placement = pos=(0,0,0.8) rot=(0,0,1;0rad)
FEATURE [App::Point] Origin156  label="Origine027"
  Role = Origin
FEATURE [App::Point] Origin158  label="Origine029"
  Role = Origin
FEATURE [PartDesign::SubShapeBinder] Binder001
  BindCopyOnChange = 0
  BindMode = 0
  ClaimChildren = false
  Context = -> Part [Body045.Binder001.]
  Fuse = false
  MakeFace = true
  OffsetFill = false
  OffsetIntersection = false
  OffsetJoinType = 0
  OffsetOpenResult = false
  PartialLoad = false
  Refine = true
  Relative = true
  Support = -> [Link[Body.Fillet001.Face1]]
  _Version = 2
FEATURE [Sketcher::SketchObject] Sketch259
  ArcFitTolerance = 1e-06
  AttachmentSupport = -> [Origin157]
  ExternalGeometry = -> [Binder001]
  ExternalTypes = [0,0,0,0]
  FullyConstrained = true
  MakeInternals = false
  MapMode = 5
  sketch-geometry (6):
    g0: LineSegment StartX=-7 StartY=17.5 StartZ=0 EndX=-7 EndY=-17.5 EndZ=0
    g1: LineSegment StartX=-7 StartY=-17.5 StartZ=0 EndX=11.5 EndY=-17.5 EndZ=0
    g2: LineSegment StartX=11.5 StartY=-17.5 StartZ=0 EndX=11.5 EndY=17.5 EndZ=0
    g3: LineSegment StartX=11.5 StartY=17.5 StartZ=0 EndX=-7 EndY=17.5 EndZ=0
    g4: Circle CenterX=-3 CenterY=13.5 CenterZ=0 NormalX=0 NormalY=0 NormalZ=1 AngleXU=0 Radius=1.7
    g5: Circle CenterX=3 CenterY=13.5 CenterZ=0 NormalX=0 NormalY=0 NormalZ=1 AngleXU=0 Radius=1.7
  constraints (16):
    c: Coincident(g0,g1)
    c: Coincident(g1,g2)
    c: Coincident(g2,g3)
    c: Coincident(g3,g0)
    c: Vertical(g0)
    c: Vertical(g2)
    c: Horizontal(g1)
    c: Horizontal(g3)
    c: PointOnObject(g-3,g0)
    c: PointOnObject(g-4,g3)
    c: Distance(g2,g-5) = 4.5
    c: DistanceY(g0,g0) = 35
    c: Coincident(g4,g-6)
    c: Diameter(g4) = 3.4
    c: Equal(g5,g4)
    c: Symmetric(g5,g4,g-2)
FEATURE [PartDesign::Pad] Pad110
  Direction = (0,0,1)
  Length = 3
  Length2 = 10
  Profile = -> Sketch259
  ReferenceAxis = -> Sketch259 [N_Axis]
  Refine = true
  Reversed = true
  SideType = 0
  Suppressed = false
  Type = 0
  Type2 = 0
FEATURE [Sketcher::SketchObject] Sketch260
  ArcFitTolerance = 1e-06
  AttachmentSupport = -> [Pad110]
  ExternalGeometry = -> [Pad110]
  ExternalTypes = [0]
  FullyConstrained = true
  MakeInternals = false
  MapMode = 5
  sketch-geometry (4):
    g0: LineSegment StartX=11.5 StartY=17.5 StartZ=0 EndX=7 EndY=17.5 EndZ=0
    g1: LineSegment StartX=7 StartY=17.5 StartZ=0 EndX=7 EndY=-17.5 EndZ=0
    g2: LineSegment StartX=7 StartY=-17.5 StartZ=0 EndX=11.5 EndY=-17.5 EndZ=0
    g3: LineSegment StartX=11.5 StartY=-17.5 StartZ=0 EndX=11.5 EndY=17.5 EndZ=0
  constraints (10):
    c: Coincident(g0,g1)
    c: Coincident(g1,g2)
    c: Coincident(g2,g3)
    c: Coincident(g3,g0)
    c: Horizontal(g0)
    c: Horizontal(g2)
    c: Vertical(g1)
    c: Coincident(g0,g-3)
    c: Coincident(g2,g-3)
    c: Distance(g0,g0) = 4.5
FEATURE [PartDesign::Pad] Pad111
  BaseFeature = -> Pad110
  Direction = (0,0,1)
  Length = 1.6
  Length2 = 10
  Profile = -> Sketch260
  ReferenceAxis = -> Sketch260 [N_Axis]
  Refine = true
  SideType = 0
  Suppressed = false
  Type = 0
  Type2 = 0
FEATURE [PartDesign::Fillet] Fillet029
  Base = -> Pad111 [Edge2,Edge1,Edge15,Edge16]
  BaseFeature = -> Pad111
  Radius = 2
  Refine = true
  SupportTransform = false
  Suppressed = false
  UseAllEdges = false
FEATURE [Sketcher::SketchObject] Sketch261
  ArcFitTolerance = 1e-06
  AttachmentSupport = -> [Fillet029]
  ExternalTypes = [0]
  FullyConstrained = true
  MakeInternals = false
  MapMode = 5
  sketch-geometry (8):
    g0: ArcOfCircle CenterX=-5.52 CenterY=13.51 CenterZ=0 NormalX=0 NormalY=0 NormalZ=1 AngleXU=0 Radius=1 StartAngle=1.5708 EndAngle=4.71239
    g1: ArcOfCircle CenterX=5.52 CenterY=13.51 CenterZ=0 NormalX=0 NormalY=0 NormalZ=1 AngleXU=0 Radius=1 StartAngle=4.71239 EndAngle=7.85398
    g2: LineSegment StartX=-5.52 StartY=14.51 StartZ=0 EndX=5.52 EndY=14.51 EndZ=0
    g3: LineSegment StartX=-5.52 StartY=12.51 StartZ=0 EndX=5.52 EndY=12.51 EndZ=0
    g4: ArcOfCircle CenterX=-5.14 CenterY=-6.53 CenterZ=0 NormalX=0 NormalY=0 NormalZ=1 AngleXU=0 Radius=1.3 StartAngle=1.5708 EndAngle=4.71239
    g5: ArcOfCircle CenterX=5.14 CenterY=-6.53 CenterZ=0 NormalX=0 NormalY=0 NormalZ=1 AngleXU=0 Radius=1.3 StartAngle=4.71239 EndAngle=7.85398
    g6: LineSegment StartX=-5.14 StartY=-5.23 StartZ=0 EndX=5.14 EndY=-5.23 EndZ=0
    g7: LineSegment StartX=-5.14 StartY=-7.83 StartZ=0 EndX=5.14 EndY=-7.83 EndZ=0
  constraints (18):
    c: Tangent(g0,g2) = 1.5708
    c: Tangent(g0,g3) = -1.5708
    c: Tangent(g1,g2) = 1.5708
    c: Tangent(g1,g3) = -1.5708
    c: Equal(g0,g1)
    c: Tangent(g4,g6) = 1.5708
    c: Tangent(g4,g7) = -1.5708
    c: Tangent(g5,g6) = 1.5708
    c: Tangent(g5,g7) = -1.5708
    c: Equal(g4,g5)
    c: DistanceY(g-1,g1) = 13.51
    c: DistanceX(g-1,g1) = 5.52
    c: Radius(g1) = 1
    c: Symmetric(g0,g1,g-2)
    c: Symmetric(g4,g5,g-2)
    c: Radius(g5) = 1.3
    c: DistanceX(g4,g5) = 10.28
    c: Distance(g5,g-1) = 6.53
FEATURE [PartDesign::Pocket] Pocket041
  BaseFeature = -> Fillet029
  Direction = (0,0,-1)
  Length = 1
  Length2 = 5
  Profile = -> Sketch261
  ReferenceAxis = -> Sketch261 [N_Axis]
  Refine = true
  SideType = 0
  Suppressed = false
  Type = 0
  Type2 = 0
FEATURE [Sketcher::SketchObject] Sketch262
  ArcFitTolerance = 1e-06
  AttachmentSupport = -> [Pocket041]
  ExternalGeometry = -> [Pocket041]
  ExternalTypes = [0]
  FullyConstrained = true
  MakeInternals = false
  MapMode = 5
  Placement = pos=(0,0,-3) rot=(1,0,0;3.14159rad)
  sketch-geometry (4):
    g0: LineSegment StartX=8.5 StartY=17.5 StartZ=0 EndX=2.5 EndY=17.5 EndZ=0
    g1: LineSegment StartX=2.5 StartY=17.5 StartZ=0 EndX=2.5 EndY=7.5 EndZ=0
    g2: LineSegment StartX=2.5 StartY=7.5 StartZ=0 EndX=8.5 EndY=7.5 EndZ=0
    g3: LineSegment StartX=8.5 StartY=7.5 StartZ=0 EndX=8.5 EndY=17.5 EndZ=0
  constraints (12):
    c: Coincident(g0,g1)
    c: Coincident(g1,g2)
    c: Coincident(g2,g3)
    c: Coincident(g3,g0)
    c: Horizontal(g0)
    c: Horizontal(g2)
    c: Vertical(g1)
    c: Vertical(g3)
    c: PointOnObject(g0,g-3)
    c: Distance(g0,g-3) = 3
    c: Distance(g0,g0) = 6
    c: DistanceY(g1,g1) = 10
FEATURE [PartDesign::Pad] Pad112
  BaseFeature = -> Pocket041
  Direction = (0,0,-1)
  Length = 10
  Length2 = 10
  Profile = -> Sketch262
  ReferenceAxis = -> Sketch262 [N_Axis]
  Refine = true
  SideType = 0
  Suppressed = false
  Type = 0
  Type2 = 0
FEATURE [PartDesign::Draft] Draft005
  Angle = 30
  Base = -> Pad112 [Face26]
  BaseFeature = -> Pad112
  NeutralPlane = -> Pad112 [Face33]
  Refine = true
  Reversed = true
  SupportTransform = false
  Suppressed = false
FEATURE [PartDesign::Fillet] Fillet030
  Base = -> Draft005 [Edge36,Edge92,Edge96]
  BaseFeature = -> Draft005
  Radius = 6
  Refine = true
  SupportTransform = false
  Suppressed = false
  UseAllEdges = false
FEATURE [PartDesign::Chamfer] Chamfer037
  Angle = 45
  Base = -> Fillet030 [Edge2]
  BaseFeature = -> Fillet030
  ChamferType = 0
  FlipDirection = false
  Refine = true
  Size = 1
  Size2 = 1
  SupportTransform = false
  Suppressed = false
  UseAllEdges = false
FEATURE [Sketcher::SketchObject] Sketch263
  ArcFitTolerance = 1e-06
  AttachmentSupport = -> [Chamfer037]
  ExternalGeometry = -> [Chamfer037]
  ExternalTypes = [0,0]
  FullyConstrained = true
  MakeInternals = false
  MapMode = 5
  Placement = pos=(8.5,0,0) rot=(0.57735,0.57735,0.57735;2.0944rad)
  sketch-geometry (1):
    g0: Circle CenterX=-11.2321 CenterY=-7 CenterZ=0 NormalX=0 NormalY=0 NormalZ=1 AngleXU=0 Radius=2.3
  constraints (2):
    c: Symmetric(g-3,g-4,g0)
    c: Diameter(g0) = 4.6
FEATURE [PartDesign::Pocket] Pocket042
  BaseFeature = -> Chamfer037
  Direction = (-1,0,0)
  Length = 10
  Length2 = 5
  Profile = -> Sketch263
  ReferenceAxis = -> Sketch263 [N_Axis]
  Refine = true
  SideType = 0
  Suppressed = false
  Type = 0
  Type2 = 0
FEATURE [PartDesign::Chamfer] Chamfer038
  Angle = 45
  Base = -> Pocket042 [Edge42,Edge67]
  BaseFeature = -> Pocket042
  ChamferType = 0
  FlipDirection = false
  Refine = true
  Size = 0.4
  Size2 = 1
  SupportTransform = false
  Suppressed = false
  UseAllEdges = false
FEATURE [PartDesign::Chamfer] Chamfer039
  Angle = 45
  Base = -> Chamfer038 [Edge50,Edge36]
  BaseFeature = -> Chamfer038
  ChamferType = 0
  FlipDirection = false
  Refine = true
  Size = 1
  Size2 = 1
  SupportTransform = false
  Suppressed = false
  UseAllEdges = false
FEATURE [PartDesign::Body] Body045  label="ColorSensorSupport"
  AllowCompound = true
  Group = -> [Sketch259,Binder001,Pad110,Sketch260,Pad111,Fillet029,Sketch261,Pocket041,Sketch262,Pad112,Draft005,Fillet030,Chamfer037,Sketch263,Pocket042,Chamfer038,Chamfer039]
  Origin = -> Origin157
  Tip = -> Chamfer039
FEATURE [App::Part] Part  label="Color_Sensor_Support"
  Group = -> [Link,Body045]
  Origin = -> Origin155
  Placement = pos=(-29,40,-30) rot=(0,1,0;4.71239rad)
FEATURE [Sketcher::SketchObject] Sketch264
  ArcFitTolerance = 1e-06
  AttachmentSupport = -> [Pocket039]
  ExternalGeometry = -> [Pocket039]
  ExternalTypes = [0,0]
  FullyConstrained = true
  MakeInternals = false
  MapMode = 5
  Placement = pos=(3.5e-15,-1.2e-15,-21.5) rot=(1,0,0;3.14159rad)
  sketch-geometry (1):
    g0: Circle CenterX=-22 CenterY=-29 CenterZ=0 NormalX=0 NormalY=0 NormalZ=1 AngleXU=0 Radius=1.5
  constraints (3):
    c: Diameter(g0) = 3
    c: Distance(g0,g-3) = 4
    c: DistanceY(g-4,g0) = 56
FEATURE [PartDesign::Pocket] Pocket043
  BaseFeature = -> Pocket039
  Direction = (0,0,1)
  Length = 5
  Length2 = 5
  Placement = pos=(3.5e-15,-1.2e-15,-10.5) rot=(0,0,1;0rad)
  Profile = -> Sketch264
  ReferenceAxis = -> Sketch264 [N_Axis]
  Refine = true
  SideType = 0
  Suppressed = false
  Type = 0
  Type2 = 0
FEATURE [PartDesign::Body] Body006  label="arm-plate"
  AllowCompound = true
  Group = -> [ShapeBinder,Sketch016,Pad005,Sketch017,Pad006,Fillet003,Sketch257,Pocket039,Sketch264,Pocket043]
  Origin = -> Origin144
  Tip = -> Pocket043
FEATURE [App::DocumentObjectGroup] Group  label="Parts"
  Group = -> [Body006,Body001,Body003,Body005,Nut001,Screw,Body004,Body,Body002,Part015,Body042,Body044,Part]
FEATURE [App::Link] Color_Sensor_Support  label="Color_Sensor_Support001"
  LinkPlacement = pos=(-44.8264,14.8243,-8.5) rot=(0.576594,0.57886,0.576594;4.19105rad)
  LinkedObject = -> Part
  Placement = pos=(-44.8264,14.8243,-8.5) rot=(0.576594,0.57886,0.576594;4.19105rad)
FEATURE [App::FeaturePython] Joint018  label="Fixed021"  # Assembly joint (typed FeaturePython)
  Angle = 0
  AngleMax = 0
  AngleMin = 0
  Detach1 = false
  Detach2 = false
  Distance = 0
  Distance2 = 0
  EnableAngleMax = false
  EnableAngleMin = false
  EnableLengthMax = false
  EnableLengthMin = false
  JointType = 0 (Fixed)
  LengthMax = 0
  LengthMin = 0
  Offset2 = pos=(0,0,0) rot=(0,0,-1;1.5708rad)
  Placement1 = pos=(8.5,-11.2321,-7) rot=(0.57735,0.57735,0.57735;2.0944rad)
  Placement2 = pos=(-22,29,-21.5) rot=(0.707107,0.707107,0;3.14159rad)
  Reference1 = -> Color_Sensor_Support [Body045.Edge39,Body045.Edge39]
  Reference2 = -> arm_plate001 [Edge39,Edge39]
  Suppressed = false
FEATURE [Assembly::JointGroup] Joints002
  Group = -> [GroundedJoint001,Joint009,Joint010,Joint011,Joint012,Joint013,Joint014,Joint015,Joint016,Joint017,Joint018]
FEATURE [Assembly::AssemblyObject] Assembly002
  Group = -> [Joints002,MG997,RoundServoHorn001,ConnecteurPneu001,Axe001,ContreRotation001,M3x10_Vis001,M8_Écrou005,SupportBras001,Coulisse001,arm_plate001,GroundedJoint001,Joint009,Joint010,Joint011,Joint012,Joint013,Joint014,Joint015,Joint016,Joint017,Color_Sensor_Support,Joint018]
  Origin = -> Origin149
  Placement = pos=(-3.2501,30.0867,30.3673) rot=(0,1,0;1.5708rad)
  Type = Assembly
FEATURE [TechDraw::DrawProjGroupItem] View001
  CoarseView = false
  Direction = (0,0,-1)
  Focus = 100
  HardHidden = false
  IsoCount = 0
  IsoHidden = false
  IsoVisible = false
  LockPosition = false
  Perspective = false
  Rotation = 0
  RotationVector = (1,0,0)
  ScaleType = 0
  ScrubCount = 1
  SeamHidden = false
  SeamVisible = false
  SmoothHidden = false
  SmoothVisible = true
  Source = -> [Pocket043]
  Type = 0
  X = 55.7673
  XDirection = (1e-16,1,0)
  Y = 167.145
FEATURE [TechDraw::DrawPage] Page  label="Feuille"
  KeepUpdated = true
  NextBalloonIndex = 1
  ProjectionType = 0
  Template = -> Template
  Views = -> [View,View001]
FEATURE [Part::Feature] Part__Feature148  label="Semelle"
  Placement = pos=(0.4,-64.9,0) rot=(0,0,1;3.14159rad)
  shape: bbox 249.2 x 217.1 x 5 mm, 134 faces (baked)
FEATURE [App::Point] Origin160  label="Origine031"
  Role = Origin
FEATURE [PartDesign::ShapeBinder] ShapeBinder001
  Placement = pos=(0.4,-64.9,0) rot=(0,0,1;3.14159rad)
  Support = -> [Part__Feature148]
  TraceSupport = false
FEATURE [Sketcher::SketchObject] Sketch265
  ArcFitTolerance = 1e-06
  AttachmentSupport = -> [ShapeBinder001]
  ExternalGeometry = -> [ShapeBinder001]
  ExternalTypes = [0,0,0,0,0,0,0,0,0]
  FullyConstrained = true
  MakeInternals = false
  MapMode = 5
  Placement = pos=(0.4,-64.9,-5) rot=(0,1,0;3.14159rad)
  sketch-geometry (12):
    g0: LineSegment [constr] StartX=0 StartY=34.0637 StartZ=0 EndX=-89.173 EndY=85.5477 EndZ=0
    g1: LineSegment [constr] StartX=0 StartY=34.0637 StartZ=0 EndX=0 EndY=106.471 EndZ=0
    g2: LineSegment StartX=0 StartY=106.471 StartZ=0 EndX=-87 EndY=106.471 EndZ=0
    g3: LineSegment StartX=-89.173 StartY=85.5477 StartZ=0 EndX=-87 EndY=89.3116 EndZ=0
    g4: LineSegment StartX=-87 StartY=89.3116 StartZ=0 EndX=-87 EndY=106.471 EndZ=0
    g5: LineSegment StartX=-89.173 StartY=85.5477 StartZ=0 EndX=-18.0263 EndY=44.4711 EndZ=0
    g6: LineSegment StartX=-18.0263 StartY=44.4711 StartZ=0 EndX=0 EndY=44.4711 EndZ=0
    g7: LineSegment StartX=0 StartY=44.4711 StartZ=0 EndX=0 EndY=106.471 EndZ=0
    g8: Circle CenterX=-69.1025 CenterY=80.3109 CenterZ=0 NormalX=0 NormalY=0 NormalZ=1 AngleXU=0 Radius=3.5
    g9: Circle CenterX=-34.4615 CenterY=60.3109 CenterZ=0 NormalX=0 NormalY=0 NormalZ=1 AngleXU=0 Radius=3.5
    g10: Circle CenterX=-51.782 CenterY=70.3109 CenterZ=0 NormalX=0 NormalY=0 NormalZ=1 AngleXU=0 Radius=1.7
    g11: Circle CenterX=-25.8013 CenterY=55.3109 CenterZ=0 NormalX=0 NormalY=0 NormalZ=1 AngleXU=0 Radius=1.7
  constraints (31):
    c: PointOnObject(g0,g-2)
    c: Coincident(g1,g0)
    c: PointOnObject(g1,g-2)
    c: Parallel(g0,g-8)
    c: Distance(g0,g-9) = 2
    c: Distance(g1,g-10) = 47
    c: Coincident(g2,g1)
    c: Horizontal(g2)
    c: PointOnObject(g0,g-11)
    c: Coincident(g3,g0)
    c: PointOnObject(g3,g-11)
    c: Coincident(g4,g3)
    c: Coincident(g4,g2)
    c: Vertical(g4)
    c: DistanceX(g2,g2) = 87
    c: Coincident(g5,g0)
    c: PointOnObject(g5,g0)
    c: Coincident(g6,g5)
    c: PointOnObject(g6,g1)
    c: Coincident(g7,g6)
    c: Coincident(g7,g1)
    c: Horizontal(g6)
    c: Distance(g-10,g6) = 15
    c: Coincident(g8,g-3)
    c: Coincident(g9,g-5)
    c: Equal(g8,g9)
    c: Diameter(g8) = 7
    c: Coincident(g10,g-4)
    c: Coincident(g11,g-6)
    c: Equal(g11,g10)
    c: Diameter(g10) = 3.4
FEATURE [PartDesign::Pad] Pad113
  Direction = (0,0,-1)
  Length = 3
  Length2 = 10
  Placement = pos=(0.4,-64.9,0) rot=(0,0,1;3.14159rad)
  Profile = -> Sketch265
  ReferenceAxis = -> Sketch265 [N_Axis]
  Refine = true
  SideType = 0
  Suppressed = false
  Type = 0
  Type2 = 0
FEATURE [PartDesign::Fillet] Fillet031
  Base = -> Pad113 [Edge11]
  BaseFeature = -> Pad113
  Placement = pos=(0.4,-64.9,0) rot=(0,0,1;3.14159rad)
  Radius = 6
  Refine = true
  SupportTransform = false
  Suppressed = false
  UseAllEdges = false
FEATURE [PartDesign::Fillet] Fillet032
  Base = -> Fillet031 [Edge31,Edge29]
  BaseFeature = -> Fillet031
  Placement = pos=(0.4,-64.9,0) rot=(0,0,1;3.14159rad)
  Radius = 3
  Refine = true
  SupportTransform = false
  Suppressed = false
  UseAllEdges = false
FEATURE [PartDesign::Fillet] Fillet033
  Base = -> Fillet032 [Edge30]
  BaseFeature = -> Fillet032
  Placement = pos=(0.4,-64.9,0) rot=(0,0,1;3.14159rad)
  Radius = 20
  Refine = true
  SupportTransform = false
  Suppressed = false
  UseAllEdges = false
FEATURE [Sketcher::SketchObject] Sketch266
  ArcFitTolerance = 1e-06
  AttachmentSupport = -> [Fillet033]
  ExternalGeometry = -> [ShapeBinder001,Fillet033]
  ExternalTypes = [0,0,0,0,0]
  FullyConstrained = true
  MakeInternals = false
  MapMode = 5
  Placement = pos=(0.4,-64.9,-5) rot=(0,0,1;3.14159rad)
  sketch-geometry (5):
    g0: LineSegment StartX=1.3e-14 StartY=-106.471 StartZ=0 EndX=7.3e-15 EndY=-59.4711 EndZ=0
    g1: LineSegment StartX=7.3e-15 StartY=-59.4711 StartZ=0 EndX=-11.6673 EndY=-59.4711 EndZ=0
    g2: LineSegment StartX=-14.1673 StartY=-60.141 StartZ=0 EndX=-75.8689 EndY=-95.7644 EndZ=0
    g3: LineSegment StartX=1.3e-14 StartY=-106.471 StartZ=0 EndX=-73 EndY=-106.471 EndZ=0
    g4: ArcOfCircle CenterX=-73 CenterY=-100.733 CenterZ=0 NormalX=0 NormalY=0 NormalZ=1 AngleXU=0 Radius=5.73771 StartAngle=2.0944 EndAngle=4.71239
  constraints (11):
    c: Coincident(g-7,g0)
    c: PointOnObject(g0,g-6)
    c: Coincident(g0,g1)
    c: Coincident(g1,g-5)
    c: Horizontal(g1)
    c: Tangent(g-4,g2) = -1.5708
    c: Coincident(g3,g0)
    c: PointOnObject(g3,g-7)
    c: Tangent(g4,g2) = -1.5708
    c: Tangent(g4,g3) = 1.5708
    c: DistanceX(g-7,g3) = 8
FEATURE [PartDesign::Pad] Pad114
  BaseFeature = -> Fillet033
  Direction = (0,0,1)
  Length = 4
  Length2 = 10
  Placement = pos=(0.4,-64.9,0) rot=(0,0,1;3.14159rad)
  Profile = -> Sketch266
  ReferenceAxis = -> Sketch266 [N_Axis]
  Refine = true
  SideType = 0
  Suppressed = false
  Type = 0
  Type2 = 0
FEATURE [PartDesign::Mirrored] Mirrored001
  BaseFeature = -> Pad114
  MirrorPlane = -> Sketch265 [V_Axis]
  Originals = -> [Pad113,Fillet031,Fillet032,Fillet033,Pad114]
  Placement = pos=(0.4,-64.9,0) rot=(0,0,1;3.14159rad)
  Refine = true
  Suppressed = false
  TransformMode = 1
FEATURE [PartDesign::Chamfer] Chamfer040
  Angle = 45
  Base = -> Mirrored001 [Edge92,Edge94,Edge96,Edge98]
  BaseFeature = -> Mirrored001
  ChamferType = 0
  FlipDirection = false
  Placement = pos=(0.4,-64.9,0) rot=(0,0,1;3.14159rad)
  Refine = true
  Size = 2
  Size2 = 1
  SupportTransform = false
  Suppressed = false
  UseAllEdges = false
FEATURE [PartDesign::Body] Body046  label="Butée"
  AllowCompound = true
  Group = -> [ShapeBinder001,Sketch265,Pad113,Fillet031,Fillet032,Fillet033,Sketch266,Pad114,Mirrored001,Chamfer040]
  Origin = -> Origin159
  Placement = pos=(0,0,-2.63) rot=(0,0,1;0rad)
  Tip = -> Chamfer040
FEATURE [Assembly::AssemblyObject] Assembly  label="twin-actuator-asm"
  Group = -> [Joints,Assembly001,Assembly002,linear_lifter_asm,GroundedJoint002,servo_support,Body046,Part__Feature148]
  Origin = -> Origin146
  Type = Assembly
note: 1 file-system path scrubbed to <path> (originals preserved in the JSON sidecar)

RESOLVED EXTERNAL PARTS (link-assembly join: the EXTERNAL_REF files above that resolve inside this repo's crawl, each included once):
---- part ../../ECAD/color-sensor-2026/color-sensor-asm.FCStd = doc fcstd_ee5536d2f9a6 ----
FCSTD DOCUMENT  (FreeCAD 1.2R20260429 (Git shallow))
Label: color-sensor-asm
License: All rights reserved
objects: App::Point×3, PartDesign::ShapeBinder×3, App::Part×2, PartDesign::Fillet×2, PartDesign::Chamfer×2, App::VRMLObject×1, Sketcher::SketchObject×1, PartDesign::Pad×1, PartDesign::Body×1
note: 21 computed .brp shape members not serialized (recipe doc carries the construction recipe); baked Part::Feature solids carry a one-line shape summary decoded from their .brp

FEATURE [App::Point] Origin001  label="Origine"
  Role = Origin
FEATURE [App::VRMLObject] color_sensor_2026  label="color-sensor-2026"
FEATURE [App::Part] Part  label="PCB-Color-Sensor"
  Group = -> [color_sensor_2026]
  Origin = -> Origin006
FEATURE [App::Point] Origin007  label="Origine006"
  Role = Origin
FEATURE [PartDesign::ShapeBinder] ShapeBinder
  TraceSupport = false
FEATURE [PartDesign::ShapeBinder] ShapeBinder001
  Placement = pos=(2.066,13.5,-0.405) rot=(0,0,1;0rad)
  TraceSupport = false
FEATURE [PartDesign::ShapeBinder] ShapeBinder002
  Placement = pos=(0,6.98,1.595) rot=(0,0,1;3.14159rad)
  TraceSupport = false
FEATURE [Sketcher::SketchObject] Sketch
  ArcFitTolerance = 1e-06
  AttachmentSupport = -> [Origin]
  ExternalGeometry = -> [ShapeBinder,ShapeBinder001,ShapeBinder002]
  ExternalTypes = [0,0,0,0,0,0,0,0,0,0]
  FullyConstrained = true
  MakeInternals = false
  MapMode = 5
  sketch-geometry (11):
    g0: Circle CenterX=-3 CenterY=13.5 CenterZ=0 NormalX=0 NormalY=0 NormalZ=1 AngleXU=0 Radius=2.3
    g1: Circle CenterX=3.766 CenterY=13.5 CenterZ=0 NormalX=0 NormalY=0 NormalZ=1 AngleXU=0 Radius=2.834
    g2: LineSegment StartX=7 StartY=15.5 StartZ=0 EndX=7 EndY=3.055 EndZ=0
    g3: LineSegment StartX=7 StartY=3.055 StartZ=0 EndX=-7 EndY=3.055 EndZ=0
    g4: LineSegment StartX=-7 StartY=3.055 StartZ=0 EndX=-7 EndY=15.5 EndZ=0
    g5: LineSegment [constr] StartX=-2.425 StartY=4.555 StartZ=0 EndX=2.425 EndY=9.405 EndZ=0
    g6: LineSegment StartX=-6 StartY=9.905 StartZ=0 EndX=-6 EndY=4.055 EndZ=0
    g7: LineSegment StartX=-6 StartY=4.055 StartZ=0 EndX=6 EndY=4.055 EndZ=0
    g8: LineSegment StartX=6 StartY=4.055 StartZ=0 EndX=6 EndY=9.905 EndZ=0
    g9: LineSegment StartX=6 StartY=9.905 StartZ=0 EndX=-6 EndY=9.905 EndZ=0
    g10: GeomPoint [constr] X=-3e-16 Y=6.98 Z=0
  constraints (26):
    c: Coincident(g0,g-3)
    c: Diameter(g0) = 4.6
    c: Coincident(g1,g-10)
    c: Coincident(g2,g-8)
    c: PointOnObject(g2,g-8)
    c: Coincident(g3,g2)
    c: PointOnObject(g3,g-4)
    c: Horizontal(g3)
    c: Coincident(g4,g3)
    c: Coincident(g4,g-5)
    c: Distance(g-12,g3) = 1.5
    c: Distance(g1,g2) = 0.4
    c: Coincident(g5,g-12)
    c: Coincident(g5,g-11)
    c: Coincident(g6,g7)
    c: Coincident(g7,g8)
    c: Coincident(g8,g9)
    c: Coincident(g9,g6)
    c: Vertical(g6)
    c: Vertical(g8)
    c: Horizontal(g7)
    c: Horizontal(g9)
    c: Symmetric(g8,g6,g10)
    c: Symmetric(g5,g5,g10)
    c: Distance(g8,g2) = 1
    c: Distance(g3,g7) = 1
FEATURE [PartDesign::Pad] Pad
  Direction = (0,0,1)
  Length = 6
  Length2 = 10
  Profile = -> Sketch
  ReferenceAxis = -> Sketch [N_Axis]
  Refine = true
  SideType = 0
  Suppressed = false
  Type = 0
  Type2 = 0
FEATURE [PartDesign::Fillet] Fillet
  Base = -> Pad [Edge26,Edge23,Edge19,Edge20]
  BaseFeature = -> Pad
  Radius = 1
  Refine = true
  SupportTransform = false
  Suppressed = false
  UseAllEdges = false
FEATURE [PartDesign::Chamfer] Chamfer
  Angle = 45
  Base = -> Fillet [Edge19,Edge36]
  BaseFeature = -> Fillet
  ChamferType = 0
  FlipDirection = false
  Refine = true
  Size = 0.4
  Size2 = 1
  SupportTransform = false
  Suppressed = false
  UseAllEdges = false
FEATURE [PartDesign::Chamfer] Chamfer001
  Angle = 45
  Base = -> Chamfer [Edge48]
  BaseFeature = -> Chamfer
  ChamferType = 0
  FlipDirection = false
  Refine = true
  Size = 0.3
  Size2 = 1
  SupportTransform = false
  Suppressed = false
  UseAllEdges = false
FEATURE [PartDesign::Fillet] Fillet001
  Base = -> Chamfer001 [Edge48,Edge47]
  BaseFeature = -> Chamfer001
  Radius = 1.8
  Refine = true
  SupportTransform = false
  Suppressed = false
  UseAllEdges = false
FEATURE [PartDesign::Body] Body  label="cache-color-sensor"
  AllowCompound = true
  Group = -> [Sketch,ShapeBinder,ShapeBinder001,ShapeBinder002,Pad,Fillet,Chamfer,Chamfer001,Fillet001]
  Origin = -> Origin
  Placement = pos=(0,0,0.8) rot=(0,0,1;0rad)
  Tip = -> Fillet001
FEATURE [App::Part] Part001  label="Color_Sensor_ASM"
  Group = -> [Body,Part]
  Origin = -> Origin008
FEATURE [App::Point] Origin009  label="Origine008"
  Role = Origin
---- part linear-lifter.FCStd = doc fcstd_d733ab31d365 ----
FCSTD DOCUMENT  (FreeCAD 1.2R20260106 (Git shallow))
Label: linear-lifter
License: All rights reserved
LicenseURL: https://en.wikipedia.org/wiki/All_rights_reserved
objects: App::FeaturePython×18, Part::Feature×15, App::Link×15, App::Point×5, App::Part×4, Assembly::JointGroup×1, Assembly::AssemblyObject×1
note: 15 computed .brp shape members not serialized (recipe doc carries the construction recipe); baked Part::Feature solids carry a one-line shape summary decoded from their .brp

FEATURE [Part::Feature] Part__Feature  label="ServoLifterPlate"
  Placement = pos=(-8,0,0) rot=(0,0,1;0rad)
  shape: bbox 3 x 61.65 x 60.3 mm, 21 faces (baked)
FEATURE [Part::Feature] Part__Feature001  label="ServoLifterSpacer"
  Placement = pos=(-8,0,0) rot=(0,0,1;0rad)
  shape: bbox 9 x 23 x 54 mm, 56 faces (baked)
FEATURE [Part::Feature] Part__Feature006  label="RoundServoHorn"
  Placement = pos=(2.274e-13,-5.72205e-06,3.05176e-05) rot=(0.171088,0.970288,0.171088;1.60095rad)
  shape: bbox 5.4 x 20 x 20 mm, 12 faces (baked)
FEATURE [Part::Feature] Part__Feature007  label="CoreMF83"
  shape: bbox 9.2 x 3 x 9.2 mm, 6 faces (baked)
FEATURE [Part::Feature] Part__Feature008  label="CoreMF001"
  shape: bbox 4.2 x 3 x 4.2 mm, 4 faces (baked)
FEATURE [App::Part] CoreMF83  label="CoreMF002"
  Group = -> [Part__Feature007,Part__Feature008]
  Origin = -> Origin002
FEATURE [App::Point] Origin003  label="Origine002"
  Role = Origin
FEATURE [Part::Feature] Part__Feature009  label="SleeveMF83"
  shape: bbox 6.8 x 2.8 x 6.8 mm, 4 faces (baked)
FEATURE [App::Part] MF83
  Group = -> [CoreMF83,Part__Feature009]
  Origin = -> Origin004
  Placement = pos=(-2.2769e-05,18,-100) rot=(0,0,1;1.5708rad)
FEATURE [App::Point] Origin005  label="Origine004"
  Role = Origin
FEATURE [Part::Feature] Part__Feature010  label="Bielle"
  Placement = pos=(3,-3.8147e-06,0) rot=(0,0,1;0rad)
  shape: bbox 3 x 35.5 x 117.5 mm, 18 faces (baked)
FEATURE [Part::Feature] Part__Feature011  label="Bielle001"
  shape: bbox 3 x 35.5 x 117.5 mm, 18 faces (baked)
FEATURE [Part::Feature] Part__Feature017  label="Body028"
  shape: bbox 3.367 x 16.32 x 116.5 mm, 9 faces (baked)
FEATURE [Part::Feature] Part__Feature018  label="ServoBody001"
  Placement = pos=(0,0,-1) rot=(0,0,1;0rad)
  shape: bbox 54 x 20 x 41 mm, 25 faces (baked)
FEATURE [Part::Feature] Part__Feature019  label="ServoAxis001"
  shape: bbox 6 x 6 x 10 mm, 4 faces (baked)
FEATURE [App::Part] MG996
  Group = -> [Part__Feature018,Part__Feature019]
  Origin = -> Origin018
  Placement = pos=(-7.6294e-06,1.90735e-06,-3.05176e-05) rot=(0.707107,0,0.707107;3.14159rad)
FEATURE [App::Point] Origin019  label="Origine018"
  Role = Origin
FEATURE [Part::Feature] Part__Feature020  label="ClipRail"
  Placement = pos=(0,-2.57492e-05,216) rot=(0,0,1;0rad)
  shape: bbox 15.57 x 32.93 x 20 mm, 24 faces (baked)
FEATURE [Part::Feature] Part__Feature023  label="MGN9-225mm-Custom"
  Placement = pos=(55.9666,32.8897,2.46922) rot=(0.447214,0.774597,-0.447214;1.82348rad)
  shape: bbox 9.729 x 10.64 x 225 mm, 62 faces (baked)
FEATURE [Part::Feature] Part__Feature024  label="mgn9c"
  Placement = pos=(8.01086e-05,-7.99998,1.62202e-06) rot=(1,0,0;0rad)
  shape: bbox 28.92 x 8.018 x 20.02 mm, 85 faces (baked)
FEATURE [Part::Feature] Part__Feature025  label="Chariot"
  shape: bbox 48 x 10 x 38 mm, 35 faces (baked)
FEATURE [App::Part] Lifter  label="linear-lifter-parts"
  Group = -> [Part__Feature,Part__Feature001,Part__Feature006,Part__Feature010,Part__Feature011,MF83,Part__Feature017,Part__Feature024,Part__Feature025,Part__Feature020,Part__Feature023,MG996]
  Origin = -> Origin028
FEATURE [App::Point] Origin029  label="Origine028"
  Role = Origin
FEATURE [App::Point] Origin030  label="Origine"
  Role = Origin
FEATURE [App::Link] MGN9_225mm_Custom  label="MGN9-225mm-Custom001"
  LinkPlacement = pos=(0,0,0) rot=(0,1,0;1.5708rad)
  LinkedObject = -> Part__Feature023
  Placement = pos=(0,0,0) rot=(0,1,0;1.5708rad)
FEATURE [App::FeaturePython] GroundedJoint  # Assembly grounded joint (typed FeaturePython)
  ObjectToGround = -> MGN9_225mm_Custom
FEATURE [App::Link] ClipRail  label="ClipRail001"
  LinkPlacement = pos=(0.499992,-64.9133,133.531) rot=(0.5,0.866025,0;3.14159rad)
  LinkedObject = -> Part__Feature020
  Placement = pos=(0.499992,-64.9133,133.531) rot=(0.5,0.866025,0;3.14159rad)
FEATURE [App::Link] ClipRail001  label="ClipRail002"
  LinkPlacement = pos=(0.499992,-64.9133,213.531) rot=(0,0,1;1.0472rad)
  LinkedObject = -> Part__Feature020
  Placement = pos=(0.499992,-64.9133,213.531) rot=(0,0,1;1.0472rad)
FEATURE [App::Link] ClipRail002  label="ClipRail003"
  LinkPlacement = pos=(0.499992,-64.9133,53.5308) rot=(0.5,0.866025,0;3.14159rad)
  LinkedObject = -> Part__Feature020
  Placement = pos=(0.499992,-64.9133,53.5308) rot=(0.5,0.866025,0;3.14159rad)
FEATURE [App::Link] Chariot  label="Chariot001"
  LinkPlacement = pos=(0.499992,-4.91335,67.3673) rot=(0,-1,0;1.5708rad)
  LinkedObject = -> Part__Feature025
  Placement = pos=(0.499992,-4.91335,67.3673) rot=(0,-1,0;1.5708rad)
FEATURE [App::Link] mgn9c  label="mgn9c001"
  LinkPlacement = pos=(0.499992,-12.9133,67.3673) rot=(0,1,0;1.5708rad)
  LinkedObject = -> Part__Feature024
  Placement = pos=(0.499992,-12.9133,67.3673) rot=(0,1,0;1.5708rad)
FEATURE [App::Link] Body028  label="Body029"
  LinkPlacement = pos=(-31.3959,8.30559,185.591) rot=(-0.157315,-0.090826,0.983363;1.06179rad)
  LinkedObject = -> Part__Feature017
  Placement = pos=(-31.3959,8.30559,185.591) rot=(-0.157315,-0.090826,0.983363;1.06179rad)
FEATURE [App::Link] MF001
  LinkPlacement = pos=(-28.0959,14.0214,185.591) rot=(0.092352,0.344662,-0.934173;0.558662rad)
  LinkedObject = -> MF83
  Placement = pos=(-28.0959,14.0214,185.591) rot=(0.092352,0.344662,-0.934173;0.558662rad)
FEATURE [App::Link] MF002
  LinkPlacement = pos=(-31.0959,8.8252,185.591) rot=(0.961552,-0.257647,-0.095058;3.19252rad)
  LinkedObject = -> MF83
  Placement = pos=(-31.0959,8.8252,185.591) rot=(0.961552,-0.257647,-0.095058;3.19252rad)
FEATURE [App::Link] Bielle001  label="Bielle002"
  LinkPlacement = pos=(2.64807,-7.19277,280.131) rot=(0.167978,0.096982,0.981009;1.06388rad)
  LinkedObject = -> Part__Feature011
  Placement = pos=(2.64807,-7.19277,280.131) rot=(0.167978,0.096982,0.981009;1.06388rad)
FEATURE [App::Link] RoundServoHorn  label="RoundServoHorn001"
  LinkPlacement = pos=(1.14807,-9.79085,280.131) rot=(0.250983,0.666109,0.702358;2.91122rad)
  LinkedObject = -> Part__Feature006
  Placement = pos=(1.14807,-9.79085,280.131) rot=(0.250983,0.666109,0.702358;2.91122rad)
FEATURE [App::Link] ServoLifterSpacer  label="ServoLifterSpacer001"
  LinkPlacement = pos=(-2.85193,-16.719,280.131) rot=(0,0,1;1.0472rad)
  LinkedObject = -> Part__Feature001
  Placement = pos=(-2.85193,-16.719,280.131) rot=(0,0,1;1.0472rad)
FEATURE [App::Link] ServoLifterPlate  label="ServoLifterPlate001"
  LinkPlacement = pos=(-2.85193,-16.719,280.131) rot=(0,0,1;1.0472rad)
  LinkedObject = -> Part__Feature
  Placement = pos=(-2.85193,-16.719,280.131) rot=(0,0,1;1.0472rad)
FEATURE [App::FeaturePython] Joint  label="Fixed"  # Assembly joint (typed FeaturePython)
  Angle = 0
  AngleMax = 0
  AngleMin = 0
  Detach1 = false
  Detach2 = false
  Distance = 0
  Distance2 = 0
  EnableAngleMax = false
  EnableAngleMin = false
  EnableLengthMax = false
  EnableLengthMin = false
  JointType = 0 (Fixed)
  LengthMax = 0
  LengthMin = 0
  Offset2 = pos=(0,0,0) rot=(0,0,-1;1.5708rad)
  Placement1 = pos=(43.3013,25,0) rot=(0.377964,0.654654,0.654654;2.41886rad)
  Placement2 = pos=(-213.531,-14.9133,0.499992) rot=(0.57735,0.57735,-0.57735;2.0944rad)
  Reference1 = -> Assembly [ClipRail001.Edge55,ClipRail001.Edge55]
  Reference2 = -> Assembly [MGN9_225mm_Custom.Edge42,MGN9_225mm_Custom.Edge42]
  Suppressed = false
FEATURE [App::FeaturePython] Joint001  label="Fixed001"  # Assembly joint (typed FeaturePython)
  Angle = 0
  AngleMax = 0
  AngleMin = 0
  Detach1 = false
  Detach2 = false
  Distance = 0
  Distance2 = 0
  EnableAngleMax = false
  EnableAngleMin = false
  EnableLengthMax = false
  EnableLengthMin = false
  JointType = 0 (Fixed)
  LengthMax = 0
  LengthMin = 0
  Offset2 = pos=(0,0,0) rot=(0,0,1;1.5708rad)
  Placement1 = pos=(43.3013,25,0) rot=(-0.377964,-0.654654,-0.654654;3.86433rad)
  Placement2 = pos=(-133.531,-14.9133,0.499992) rot=(0.57735,-0.57735,0.57735;2.0944rad)
  Reference1 = -> Assembly [ClipRail.Edge55,ClipRail.Edge55]
  Reference2 = -> Assembly [MGN9_225mm_Custom.Edge30,MGN9_225mm_Custom.Edge30]
  Suppressed = false
FEATURE [App::FeaturePython] Joint002  label="Fixed002"  # Assembly joint (typed FeaturePython)
  Angle = 0
  AngleMax = 0
  AngleMin = 0
  Detach1 = false
  Detach2 = false
  Distance = 0
  Distance2 = 0
  EnableAngleMax = false
  EnableAngleMin = false
  EnableLengthMax = false
  EnableLengthMin = false
  JointType = 0 (Fixed)
  LengthMax = 0
  LengthMin = 0
  Placement1 = pos=(43.3013,25,0) rot=(-0.377964,-0.654654,-0.654654;3.86433rad)
  Placement2 = pos=(-53.5308,-14.9133,0.499992) rot=(-0.57735,-0.57735,-0.57735;2.0944rad)
  Reference1 = -> Assembly [ClipRail002.Edge55,ClipRail002.Edge55]
  Reference2 = -> Assembly [MGN9_225mm_Custom.Edge51,MGN9_225mm_Custom.Edge51]
  Suppressed = false
FEATURE [App::FeaturePython] Joint003  label="Slider003"  # Assembly joint (typed FeaturePython)
  Angle = 0
  AngleMax = 0
  AngleMin = 0
  Detach1 = false
  Detach2 = false
  Distance = 0
  Distance2 = 0
  EnableAngleMax = false
  EnableAngleMin = false
  EnableLengthMax = false
  EnableLengthMin = false
  JointType = 3 (Slider)
  LengthMax = 0
  LengthMin = 0
  Placement1 = pos=(-14.45,2.5,-4.8) rot=(0,-1,0;1.5708rad)
  Placement2 = pos=(-1.03078,-10.4133,-4.30001) rot=(0.707107,0,0.707107;3.14159rad)
  Reference1 = -> Assembly [mgn9c.Face26,mgn9c.Edge6]
  Reference2 = -> Assembly [MGN9_225mm_Custom.Edge97,MGN9_225mm_Custom.Edge97]
  Suppressed = false
FEATURE [App::FeaturePython] Joint004  label="Fixed003"  # Assembly joint (typed FeaturePython)
  Angle = 0
  AngleMax = 0
  AngleMin = 0
  Detach1 = false
  Detach2 = false
  Distance = 0
  Distance2 = 0
  EnableAngleMax = false
  EnableAngleMin = false
  EnableLengthMax = false
  EnableLengthMin = false
  JointType = 0 (Fixed)
  LengthMax = 0
  LengthMin = 0
  Offset2 = pos=(0,0,0) rot=(0,0,1;1.5708rad)
  Placement1 = pos=(-5,3.6e-15,7.5) rot=(0,-0.707107,-0.707107;3.14159rad)
  Placement2 = pos=(5,8,-7.5) rot=(-1,0,0;1.5708rad)
  Reference1 = -> Assembly [Chariot.Edge5,Chariot.Edge5]
  Reference2 = -> Assembly [mgn9c.Edge190,mgn9c.Edge190]
  Suppressed = false
FEATURE [App::FeaturePython] Joint005  label="Revolute004"  # Assembly joint (typed FeaturePython)
  Angle = 0
  AngleMax = 0
  AngleMin = 0
  Detach1 = false
  Detach2 = false
  Distance = 0
  Distance2 = 0
  EnableAngleMax = false
  EnableAngleMin = false
  EnableLengthMax = false
  EnableLengthMin = false
  JointType = 1 (Revolute)
  LengthMax = 0
  LengthMin = 0
  Placement1 = pos=(-1.8e-15,-3.6e-15,-105) rot=(0.57735,0.57735,0.57735;2.0944rad)
  Placement2 = pos=(15,3.60289,15.2404) rot=(-1,0,0;5.23599rad)
  Reference1 = -> Assembly [Body028.Edge10,Body028.Edge10]
  Reference2 = -> Assembly [Chariot.Edge31,Chariot.Edge31]
  Suppressed = false
FEATURE [App::Link] Bielle002  label="Bielle003"
  LinkPlacement = pos=(1.14807,-9.79085,280.131) rot=(0.167978,0.096982,0.981009;1.06388rad)
  LinkedObject = -> Part__Feature011
  Placement = pos=(1.14807,-9.79085,280.131) rot=(0.167978,0.096982,0.981009;1.06388rad)
FEATURE [App::FeaturePython] Joint006  label="Fixed004"  # Assembly joint (typed FeaturePython)
  Angle = 0
  AngleMax = 0
  AngleMin = 0
  Detach1 = false
  Detach2 = false
  Distance = 0
  Distance2 = 0
  EnableAngleMax = false
  EnableAngleMin = false
  EnableLengthMax = false
  EnableLengthMin = false
  JointType = 0 (Fixed)
  LengthMax = 0
  LengthMin = 0
  Placement1 = pos=(3,18,-100) rot=(0.57735,0.57735,0.57735;2.0944rad)
  Placement2 = pos=(-2.13e-14,18,-100) rot=(0.57735,0.57735,0.57735;2.0944rad)
  Reference1 = -> Assembly [Bielle002.Edge31,Bielle002.Edge31]
  Reference2 = -> Assembly [Bielle001.Edge14,Bielle001.Edge14]
  Suppressed = false
FEATURE [App::FeaturePython] Joint008  label="Fixed006"  # Assembly joint (typed FeaturePython)
  Angle = 0
  AngleMax = 0
  AngleMin = 0
  Detach1 = false
  Detach2 = false
  Distance = 0
  Distance2 = 0
  EnableAngleMax = false
  EnableAngleMin = false
  EnableLengthMax = false
  EnableLengthMin = false
  JointType = 0 (Fixed)
  LengthMax = 0
  LengthMin = 0
  Placement1 = pos=(0,0,0) rot=(0,0.707107,0.707107;3.14159rad)
  Placement2 = pos=(3,18,-100) rot=(0.57735,0.57735,0.57735;2.0944rad)
  Reference1 = -> Assembly [MF001.CoreMF83.Part__Feature007.Edge9,MF001.CoreMF83.Part__Feature007.Edge9]
  Reference2 = -> Assembly [Bielle001.Edge31,Bielle001.Edge31]
  Suppressed = false
FEATURE [App::FeaturePython] Joint009  label="Fixed007"  # Assembly joint (typed FeaturePython)
  Angle = 0
  AngleMax = 0
  AngleMin = 0
  Detach1 = false
  Detach2 = false
  Distance = 0
  Distance2 = 0
  EnableAngleMax = false
  EnableAngleMin = false
  EnableLengthMax = false
  EnableLengthMin = false
  JointType = 0 (Fixed)
  LengthMax = 0
  LengthMin = 0
  Placement1 = pos=(0,0,0) rot=(0,0.707107,0.707107;3.14159rad)
  Placement2 = pos=(-2.22e-14,18,-100) rot=(0.57735,0.57735,0.57735;2.0944rad)
  Reference1 = -> Assembly [MF002.CoreMF83.Part__Feature007.Edge9,MF002.CoreMF83.Part__Feature007.Edge9]
  Reference2 = -> Assembly [Bielle002.Edge14,Bielle002.Edge14]
  Suppressed = false
FEATURE [App::FeaturePython] Joint010  label="Revolute009"  # Assembly joint (typed FeaturePython)
  Angle = 0
  AngleMax = 0
  AngleMin = 0
  Detach1 = false
  Detach2 = false
  Distance = 0
  Distance2 = 0
  EnableAngleMax = false
  EnableAngleMin = false
  EnableLengthMax = false
  EnableLengthMin = false
  JointType = 1 (Revolute)
  LengthMax = 0
  LengthMin = 0
  Placement1 = pos=(0,0,0) rot=(0.57735,0.57735,0.57735;2.0944rad)
  Placement2 = pos=(0,0.6,0) rot=(0,0.707107,0.707107;3.14159rad)
  Reference1 = -> Assembly [Body028.Edge9,Body028.Edge9]
  Reference2 = -> Assembly [MF002.CoreMF83.Part__Feature008.Edge2,MF002.CoreMF83.Part__Feature008.Edge2]
  Suppressed = false
FEATURE [App::FeaturePython] Joint011  label="Fixed009"  # Assembly joint (typed FeaturePython)
  Angle = 0
  AngleMax = 0
  AngleMin = 0
  Detach1 = false
  Detach2 = false
  Distance = 0
  Distance2 = 0
  EnableAngleMax = false
  EnableAngleMin = false
  EnableLengthMax = false
  EnableLengthMin = false
  JointType = 0 (Fixed)
  LengthMax = 0
  LengthMin = 0
  Placement2 = pos=(0,0,0) rot=(0.57735,0.57735,0.57735;2.0944rad)
  Reference1 = -> Assembly [RoundServoHorn.Edge24,RoundServoHorn.Edge24]
  Reference2 = -> Assembly [Bielle002.Edge19,Bielle002.Edge19]
  Suppressed = false
FEATURE [App::Link] MG997
  LinkPlacement = pos=(1.14807,-9.79085,280.131) rot=(0.654654,0.377964,0.654654;3.86433rad)
  LinkedObject = -> MG996
  Placement = pos=(1.14807,-9.79085,280.131) rot=(0.654654,0.377964,0.654654;3.86433rad)
FEATURE [App::FeaturePython] Joint012  label="Fixed010"  # Assembly joint (typed FeaturePython)
  Angle = 0
  AngleMax = 0
  AngleMin = 0
  Detach1 = false
  Detach2 = false
  Distance = 0
  Distance2 = 0
  EnableAngleMax = false
  EnableAngleMin = false
  EnableLengthMax = false
  EnableLengthMin = false
  JointType = 0 (Fixed)
  LengthMax = 0
  LengthMin = 0
  Placement1 = pos=(3.6e-15,-5,14.5) rot=(0.57735,0.57735,0.57735;2.0944rad)
  Placement2 = pos=(0,-5,14.5) rot=(0.57735,0.57735,0.57735;2.0944rad)
  Reference1 = -> Assembly [ServoLifterSpacer.Edge36,ServoLifterSpacer.Edge36]
  Reference2 = -> Assembly [ServoLifterPlate.Edge16,ServoLifterPlate.Edge16]
  Suppressed = false
FEATURE [App::FeaturePython] Joint013  label="Fixed011"  # Assembly joint (typed FeaturePython)
  Angle = 0
  AngleMax = 0
  AngleMin = 0
  Detach1 = false
  Detach2 = false
  Distance = 0
  Distance2 = 0
  EnableAngleMax = false
  EnableAngleMin = false
  EnableLengthMax = false
  EnableLengthMin = false
  JointType = 0 (Fixed)
  LengthMax = 0
  LengthMin = 0
  Offset2 = pos=(0,0,0) rot=(0,0,1;1.5708rad)
  Placement1 = pos=(14.5,5,-16) rot=(0,0,1;0rad)
  Placement2 = pos=(-9,-5,14.5) rot=(0.707107,0,0.707107;3.14159rad)
  Reference1 = -> Assembly [MG997.Part__Feature018.Edge52,MG997.Part__Feature018.Edge52]
  Reference2 = -> Assembly [ServoLifterSpacer.Edge53,ServoLifterSpacer.Edge53]
  Suppressed = false
FEATURE [App::FeaturePython] Joint014  label="Revolute012"  # Assembly joint (typed FeaturePython)
  Angle = 0
  AngleMax = 0
  AngleMin = 0
  Detach1 = false
  Detach2 = false
  Distance = 0
  Distance2 = 0
  EnableAngleMax = false
  EnableAngleMin = false
  EnableLengthMax = false
  EnableLengthMin = false
  JointType = 1 (Revolute)
  LengthMax = 0
  LengthMin = 0
  Placement1 = pos=(0,0,-2) rot=(0,0,1;0rad)
  Placement2 = pos=(0,0,-2) rot=(0,0,1;0rad)
  Reference1 = -> Assembly [MG997.Part__Feature019.Edge5,MG997.Part__Feature019.Edge5]
  Reference2 = -> Assembly [RoundServoHorn.Edge22,RoundServoHorn.Edge22]
  Suppressed = false
FEATURE [App::FeaturePython] Joint015  label="Parallel012"  # Assembly joint (typed FeaturePython)
  Angle = 0
  AngleMax = 0
  AngleMin = 0
  Detach1 = false
  Detach2 = false
  Distance = 0
  Distance2 = 0
  EnableAngleMax = false
  EnableAngleMin = false
  EnableLengthMax = false
  EnableLengthMin = false
  JointType = 6 (Parallel)
  LengthMax = 0
  LengthMin = 0
  Placement1 = pos=(1.5,-10,-10) rot=(0.57735,-0.57735,-0.57735;4.18879rad)
  Placement2 = pos=(42.5,50,0) rot=(-1,0,0;1.5708rad)
  Reference1 = -> Assembly [ServoLifterPlate.Face6,ServoLifterPlate.Face6]
  Reference2 = -> Assembly [ClipRail001.Face21,ClipRail001.Face21]
  Suppressed = false
FEATURE [App::FeaturePython] Joint016  label="Distance013"  # Assembly joint (typed FeaturePython)
  Angle = 0
  AngleMax = 0
  AngleMin = 0
  Detach1 = false
  Detach2 = false
  Distance = -17.6
  Distance2 = 0
  EnableAngleMax = false
  EnableAngleMin = false
  EnableLengthMax = false
  EnableLengthMin = false
  JointType = 5 (Distance)
  LengthMax = 0
  LengthMin = 0
  Placement1 = pos=(1.5,20.5,-39) rot=(0,0,1;1.5708rad)
  Placement2 = pos=(37.8607,33.2868,10) rot=(0,0,1;0rad)
  Reference1 = -> Assembly [ServoLifterPlate.Face2,ServoLifterPlate.Face2]
  Reference2 = -> Assembly [ClipRail001.Face6,ClipRail001.Edge9]
  Suppressed = false
FEATURE [App::FeaturePython] Joint017  label="Distance014"  # Assembly joint (typed FeaturePython)
  Angle = 0
  AngleMax = 0
  AngleMin = 0
  Detach1 = false
  Detach2 = false
  Distance = -33
  Distance2 = 0
  EnableAngleMax = false
  EnableAngleMin = false
  EnableLengthMax = false
  EnableLengthMin = false
  JointType = 5 (Distance)
  LengthMax = 0
  LengthMin = 0
  Placement1 = pos=(42.5,50,0) rot=(-1,0,0;1.5708rad)
  Placement2 = pos=(1.5,-10,-10) rot=(0.57735,-0.57735,-0.57735;4.18879rad)
  Reference1 = -> Assembly [ClipRail001.Face21,ClipRail001.Face21]
  Reference2 = -> Assembly [ServoLifterPlate.Face6,ServoLifterPlate.Face6]
  Suppressed = false
FEATURE [Assembly::JointGroup] Joints
  Group = -> [GroundedJoint,Joint,Joint001,Joint002,Joint003,Joint004,Joint005,Joint006,Joint008,Joint009,Joint010,Joint011,Joint012,Joint013,Joint014,Joint015,Joint016,Joint017]
FEATURE [Assembly::AssemblyObject] Assembly  label="linear-lifter-asm"
  Group = -> [Joints,MGN9_225mm_Custom,GroundedJoint,ClipRail,ClipRail001,ClipRail002,Chariot,mgn9c,Body028,MF001,MF002,Bielle001,RoundServoHorn,ServoLifterSpacer,ServoLifterPlate,Joint,Joint001,Joint002,Joint003,Joint004,Joint005,Bielle002,Joint006,Joint008,Joint009,Joint010,Joint011,MG997,Joint012,Joint013,Joint014,Joint015,Joint016,Joint017]
  Origin = -> Origin
  Type = Assembly
